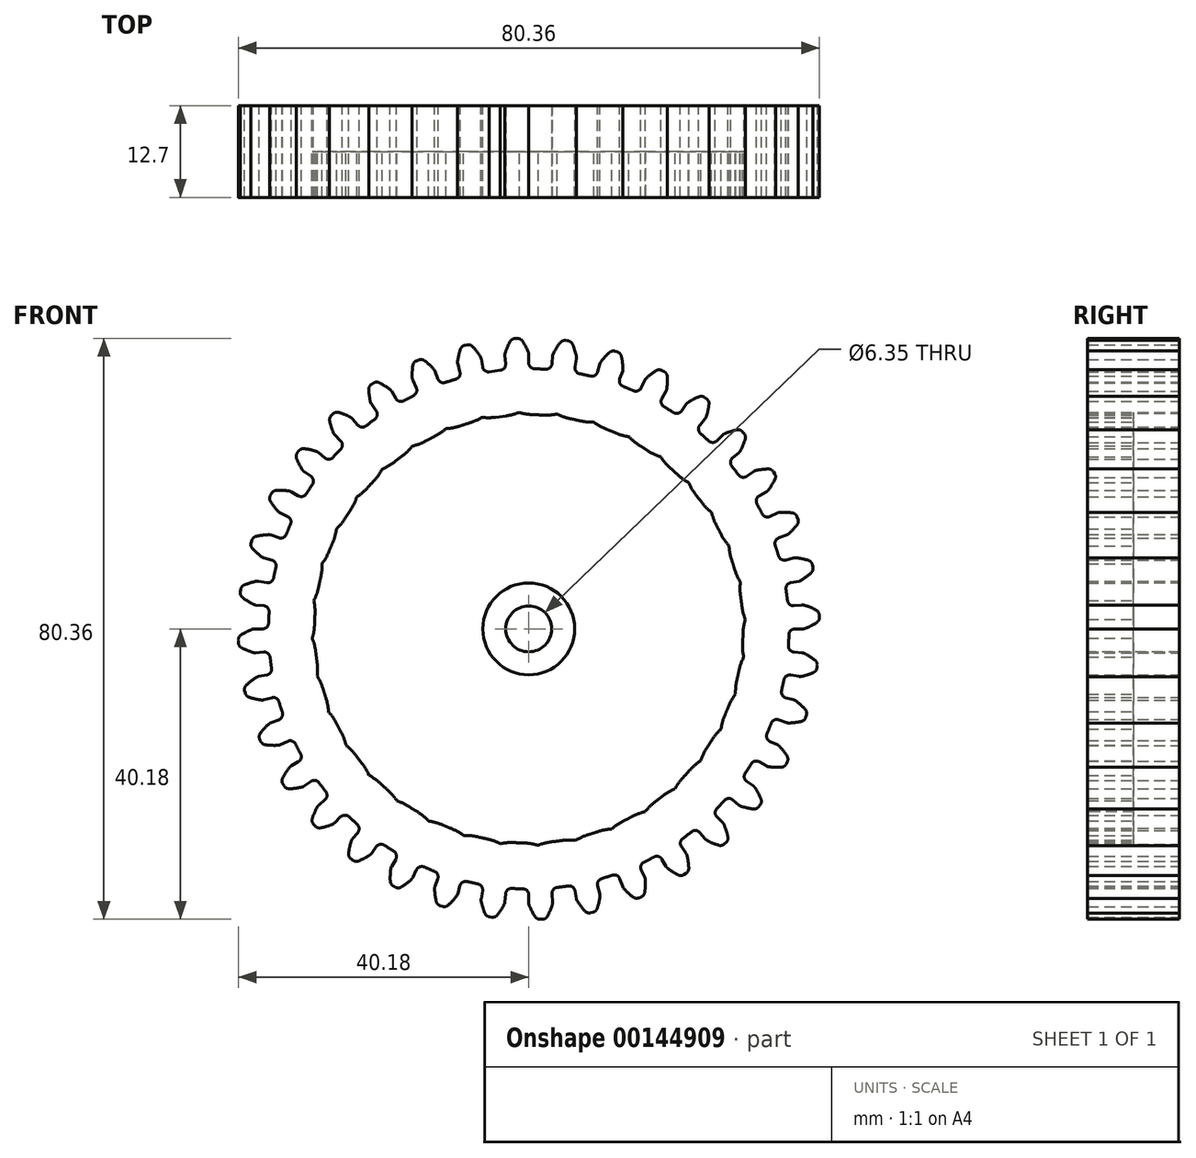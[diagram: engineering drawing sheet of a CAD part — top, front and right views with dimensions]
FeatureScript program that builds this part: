
annotation { "Feature Type Name" : "Feature", "Feature Type Description" : "" }
export const myFeature = defineFeature(function(context is Context, id is Id, definition is map)
    precondition{}
    {
        {
            var Q0;
            Q0=qCreatedBy(makeId("Front.planeOp"),FACE);
            var sketch = newSketch(context, id + "F0", { "sketchPlane" : qUnion([Q0])});
            skPoint(sketch, "E0.endSnap0", {"position": v(-3.06, 34.96) * mm});
            skArc(sketch, "E1.trimOffspring", {"start": v(-0.06, 38.25) * mm, "mid": v(-0.43, 39.05) * mm, "end": v(-0.86, 39.8) * mm});
            skLineSegment(sketch, "E2", {"start": v(0, 37.94) * mm, "end": v(0, 36.8) * mm});
            skLineSegment(sketch, "E3", {"start": v(-1.6, 40.18) * mm, "end": v(-1.75, 40.17) * mm});
            skArc(sketch, "E4.MirrorCS", {"start": v(-3.27, 38.11) * mm, "mid": v(-2.98, 38.93) * mm, "end": v(-2.61, 39.72) * mm});
            skLineSegment(sketch, "E5.MirrorCS", {"start": v(-1.91, 40.17) * mm, "end": v(-1.75, 40.17) * mm});
            skLineSegment(sketch, "E6.MirrorCS", {"start": v(-3.3, 37.8) * mm, "end": v(-3.2, 36.66) * mm});
            skPoint(sketch, "E7.visualSharp", {"position": v(0, 35.98) * mm});
            skArc(sketch, "E7.filletArc", {"start": v(0, 36.8) * mm, "mid": v(0.24, 36.22) * mm, "end": v(0.8, 35.97) * mm});
            skArc(sketch, "E8.filletArc", {"start": v(-0.86, 39.8) * mm, "mid": v(-1.18, 40.09) * mm, "end": v(-1.6, 40.18) * mm});
            skArc(sketch, "E9.filletArc", {"start": v(-1.91, 40.17) * mm, "mid": v(-2.32, 40.04) * mm, "end": v(-2.61, 39.72) * mm});
            skPoint(sketch, "E10.visualSharp", {"position": v(-3.32, 37.96) * mm});
            skArc(sketch, "E10.filletArc", {"start": v(-3.27, 38.11) * mm, "mid": v(-3.3, 37.96) * mm, "end": v(-3.3, 37.8) * mm});
            skPoint(sketch, "E11.visualSharp", {"position": v(-3.14, 35.85) * mm});
            skArc(sketch, "E11.filletArc", {"start": v(-3.94, 35.77) * mm, "mid": v(-3.4, 36.06) * mm, "end": v(-3.2, 36.66) * mm});
            skPoint(sketch, "E12.visualSharp", {"position": v(0, 38.1) * mm});
            skArc(sketch, "E12.filletArc", {"start": v(0, 37.94) * mm, "mid": v(-0.02, 38.1) * mm, "end": v(-0.06, 38.25) * mm});
            skArc(sketch, "E13.1.0", {"start": v(-10.1, 34.54) * mm, "mid": v(-9.6, 34.93) * mm, "end": v(-9.52, 35.55) * mm});
            skLineSegment(sketch, "E13.1.1", {"start": v(-9.82, 36.65) * mm, "end": v(-9.52, 35.55) * mm});
            skArc(sketch, "E13.1.2", {"start": v(-9.84, 36.97) * mm, "mid": v(-9.85, 36.8) * mm, "end": v(-9.82, 36.65) * mm});
            skArc(sketch, "E13.1.3", {"start": v(-9.84, 36.97) * mm, "mid": v(-9.7, 37.83) * mm, "end": v(-9.47, 38.67) * mm});
            skArc(sketch, "E13.1.4", {"start": v(-6.4, 36.24) * mm, "mid": v(-6.06, 35.71) * mm, "end": v(-5.45, 35.57) * mm});
            skLineSegment(sketch, "E13.1.5", {"start": v(-6.59, 37.37) * mm, "end": v(-6.4, 36.24) * mm});
            skArc(sketch, "E13.1.6", {"start": v(-6.59, 37.37) * mm, "mid": v(-6.63, 37.52) * mm, "end": v(-6.7, 37.66) * mm});
            skArc(sketch, "E13.1.7", {"start": v(-8.86, 39.22) * mm, "mid": v(-9.24, 39.03) * mm, "end": v(-9.47, 38.67) * mm});
            skArc(sketch, "E13.1.8", {"start": v(-7.76, 39.05) * mm, "mid": v(-8.12, 39.27) * mm, "end": v(-8.55, 39.3) * mm});
            skArc(sketch, "E13.1.9", {"start": v(-6.7, 37.66) * mm, "mid": v(-7.2, 38.38) * mm, "end": v(-7.76, 39.05) * mm});
            skLineSegment(sketch, "E13.1.10", {"start": v(-8.55, 39.3) * mm, "end": v(-8.7, 39.26) * mm});
            skLineSegment(sketch, "E13.1.11", {"start": v(-8.86, 39.22) * mm, "end": v(-8.7, 39.26) * mm});
            skArc(sketch, "E13.2.0", {"start": v(-15.93, 32.26) * mm, "mid": v(-15.52, 32.73) * mm, "end": v(-15.55, 33.35) * mm});
            skLineSegment(sketch, "E13.2.1", {"start": v(-16.04, 34.39) * mm, "end": v(-15.55, 33.35) * mm});
            skArc(sketch, "E13.2.2", {"start": v(-16.11, 34.7) * mm, "mid": v(-16.09, 34.54) * mm, "end": v(-16.04, 34.39) * mm});
            skArc(sketch, "E13.2.3", {"start": v(-16.11, 34.7) * mm, "mid": v(-16.12, 35.57) * mm, "end": v(-16.04, 36.44) * mm});
            skArc(sketch, "E13.2.4", {"start": v(-12.59, 34.58) * mm, "mid": v(-12.17, 34.12) * mm, "end": v(-11.55, 34.08) * mm});
            skLineSegment(sketch, "E13.2.5", {"start": v(-12.98, 35.65) * mm, "end": v(-12.59, 34.58) * mm});
            skArc(sketch, "E13.2.6", {"start": v(-12.98, 35.65) * mm, "mid": v(-13.05, 35.8) * mm, "end": v(-13.14, 35.93) * mm});
            skArc(sketch, "E13.2.7", {"start": v(-15.54, 37.09) * mm, "mid": v(-15.88, 36.83) * mm, "end": v(-16.04, 36.44) * mm});
            skArc(sketch, "E13.2.8", {"start": v(-14.42, 37.1) * mm, "mid": v(-14.82, 37.27) * mm, "end": v(-15.24, 37.21) * mm});
            skArc(sketch, "E13.2.9", {"start": v(-13.14, 35.93) * mm, "mid": v(-13.75, 36.54) * mm, "end": v(-14.42, 37.1) * mm});
            skLineSegment(sketch, "E13.2.10", {"start": v(-15.24, 37.21) * mm, "end": v(-15.39, 37.15) * mm});
            skLineSegment(sketch, "E13.2.11", {"start": v(-15.54, 37.09) * mm, "end": v(-15.39, 37.15) * mm});
            skArc(sketch, "E13.3.0", {"start": v(-21.3, 29) * mm, "mid": v(-20.97, 29.54) * mm, "end": v(-21.1, 30.14) * mm});
            skLineSegment(sketch, "E13.3.1", {"start": v(-21.76, 31.08) * mm, "end": v(-21.1, 30.14) * mm});
            skArc(sketch, "E13.3.2", {"start": v(-21.9, 31.37) * mm, "mid": v(-21.84, 31.22) * mm, "end": v(-21.76, 31.08) * mm});
            skArc(sketch, "E13.3.3", {"start": v(-21.9, 31.37) * mm, "mid": v(-22.05, 32.23) * mm, "end": v(-22.12, 33.1) * mm});
            skArc(sketch, "E13.3.4", {"start": v(-18.4, 31.87) * mm, "mid": v(-17.9, 31.49) * mm, "end": v(-17.29, 31.56) * mm});
            skLineSegment(sketch, "E13.3.5", {"start": v(-18.97, 32.86) * mm, "end": v(-18.4, 31.87) * mm});
            skArc(sketch, "E13.3.6", {"start": v(-18.97, 32.86) * mm, "mid": v(-19.06, 32.99) * mm, "end": v(-19.18, 33.1) * mm});
            skArc(sketch, "E13.3.7", {"start": v(-21.74, 33.83) * mm, "mid": v(-22.03, 33.51) * mm, "end": v(-22.12, 33.1) * mm});
            skArc(sketch, "E13.3.8", {"start": v(-20.65, 34.04) * mm, "mid": v(-21.06, 34.13) * mm, "end": v(-21.47, 34) * mm});
            skArc(sketch, "E13.3.9", {"start": v(-19.18, 33.1) * mm, "mid": v(-19.9, 33.6) * mm, "end": v(-20.65, 34.04) * mm});
            skLineSegment(sketch, "E13.3.10", {"start": v(-21.47, 34) * mm, "end": v(-21.6, 33.91) * mm});
            skLineSegment(sketch, "E13.3.11", {"start": v(-21.74, 33.83) * mm, "end": v(-21.6, 33.91) * mm});
            skArc(sketch, "E13.4.0", {"start": v(-26, 24.87) * mm, "mid": v(-25.78, 25.45) * mm, "end": v(-26.02, 26.02) * mm});
            skLineSegment(sketch, "E13.4.1", {"start": v(-26.83, 26.83) * mm, "end": v(-26.02, 26.02) * mm});
            skArc(sketch, "E13.4.2", {"start": v(-27, 27.1) * mm, "mid": v(-26.93, 26.95) * mm, "end": v(-26.83, 26.83) * mm});
            skArc(sketch, "E13.4.3", {"start": v(-27, 27.1) * mm, "mid": v(-27.3, 27.91) * mm, "end": v(-27.53, 28.75) * mm});
            skArc(sketch, "E13.4.4", {"start": v(-23.65, 28.2) * mm, "mid": v(-23.1, 27.9) * mm, "end": v(-22.5, 28.08) * mm});
            skLineSegment(sketch, "E13.4.5", {"start": v(-24.39, 29.07) * mm, "end": v(-23.65, 28.2) * mm});
            skArc(sketch, "E13.4.6", {"start": v(-24.39, 29.07) * mm, "mid": v(-24.5, 29.18) * mm, "end": v(-24.64, 29.26) * mm});
            skArc(sketch, "E13.4.7", {"start": v(-27.29, 29.54) * mm, "mid": v(-27.51, 29.18) * mm, "end": v(-27.53, 28.75) * mm});
            skArc(sketch, "E13.4.8", {"start": v(-26.24, 29.94) * mm, "mid": v(-26.67, 29.95) * mm, "end": v(-27.05, 29.76) * mm});
            skArc(sketch, "E13.4.9", {"start": v(-24.64, 29.26) * mm, "mid": v(-25.42, 29.64) * mm, "end": v(-26.24, 29.94) * mm});
            skLineSegment(sketch, "E13.4.10", {"start": v(-27.05, 29.76) * mm, "end": v(-27.17, 29.65) * mm});
            skLineSegment(sketch, "E13.4.11", {"start": v(-27.29, 29.54) * mm, "end": v(-27.17, 29.65) * mm});
            skArc(sketch, "E13.5.0", {"start": v(-29.93, 19.97) * mm, "mid": v(-29.8, 20.58) * mm, "end": v(-30.14, 21.1) * mm});
            skLineSegment(sketch, "E13.5.1", {"start": v(-31.08, 21.76) * mm, "end": v(-30.14, 21.1) * mm});
            skArc(sketch, "E13.5.2", {"start": v(-31.3, 22) * mm, "mid": v(-31.2, 21.87) * mm, "end": v(-31.08, 21.76) * mm});
            skArc(sketch, "E13.5.3", {"start": v(-31.3, 22) * mm, "mid": v(-31.74, 22.74) * mm, "end": v(-32.1, 23.53) * mm});
            skArc(sketch, "E13.5.4", {"start": v(-28.2, 23.65) * mm, "mid": v(-27.6, 23.46) * mm, "end": v(-27.04, 23.74) * mm});
            skLineSegment(sketch, "E13.5.5", {"start": v(-29.07, 24.39) * mm, "end": v(-28.2, 23.65) * mm});
            skArc(sketch, "E13.5.6", {"start": v(-29.07, 24.39) * mm, "mid": v(-29.2, 24.48) * mm, "end": v(-29.34, 24.54) * mm});
            skArc(sketch, "E13.5.7", {"start": v(-32, 24.35) * mm, "mid": v(-32.16, 23.96) * mm, "end": v(-32.1, 23.53) * mm});
            skArc(sketch, "E13.5.8", {"start": v(-31.04, 24.92) * mm, "mid": v(-31.47, 24.87) * mm, "end": v(-31.8, 24.6) * mm});
            skArc(sketch, "E13.5.9", {"start": v(-29.34, 24.54) * mm, "mid": v(-30.18, 24.77) * mm, "end": v(-31.04, 24.92) * mm});
            skLineSegment(sketch, "E13.5.10", {"start": v(-31.8, 24.6) * mm, "end": v(-31.9, 24.48) * mm});
            skLineSegment(sketch, "E13.5.11", {"start": v(-32, 24.35) * mm, "end": v(-31.9, 24.48) * mm});
            skArc(sketch, "E13.6.0", {"start": v(-32.94, 14.47) * mm, "mid": v(-32.93, 15.1) * mm, "end": v(-33.35, 15.55) * mm});
            skLineSegment(sketch, "E13.6.1", {"start": v(-34.39, 16.04) * mm, "end": v(-33.35, 15.55) * mm});
            skArc(sketch, "E13.6.2", {"start": v(-34.64, 16.22) * mm, "mid": v(-34.52, 16.12) * mm, "end": v(-34.39, 16.04) * mm});
            skArc(sketch, "E13.6.3", {"start": v(-34.64, 16.22) * mm, "mid": v(-35.2, 16.89) * mm, "end": v(-35.7, 17.6) * mm});
            skArc(sketch, "E13.6.4", {"start": v(-31.87, 18.4) * mm, "mid": v(-31.25, 18.31) * mm, "end": v(-30.75, 18.69) * mm});
            skLineSegment(sketch, "E13.6.5", {"start": v(-32.86, 18.97) * mm, "end": v(-31.87, 18.4) * mm});
            skArc(sketch, "E13.6.6", {"start": v(-32.86, 18.97) * mm, "mid": v(-33, 19.04) * mm, "end": v(-33.16, 19.07) * mm});
            skArc(sketch, "E13.6.7", {"start": v(-35.74, 18.42) * mm, "mid": v(-35.83, 18) * mm, "end": v(-35.7, 17.6) * mm});
            skArc(sketch, "E13.6.8", {"start": v(-34.9, 19.15) * mm, "mid": v(-35.3, 19.03) * mm, "end": v(-35.6, 18.71) * mm});
            skArc(sketch, "E13.6.9", {"start": v(-33.16, 19.07) * mm, "mid": v(-34.03, 19.15) * mm, "end": v(-34.9, 19.15) * mm});
            skLineSegment(sketch, "E13.6.10", {"start": v(-35.6, 18.71) * mm, "end": v(-35.67, 18.57) * mm});
            skLineSegment(sketch, "E13.6.11", {"start": v(-35.74, 18.42) * mm, "end": v(-35.67, 18.57) * mm});
            skArc(sketch, "E13.7.0", {"start": v(-34.96, 8.53) * mm, "mid": v(-35.05, 9.15) * mm, "end": v(-35.55, 9.52) * mm});
            skLineSegment(sketch, "E13.7.1", {"start": v(-36.65, 9.82) * mm, "end": v(-35.55, 9.52) * mm});
            skArc(sketch, "E13.7.2", {"start": v(-36.93, 9.96) * mm, "mid": v(-36.8, 9.88) * mm, "end": v(-36.65, 9.82) * mm});
            skArc(sketch, "E13.7.3", {"start": v(-36.93, 9.96) * mm, "mid": v(-37.6, 10.52) * mm, "end": v(-38.22, 11.13) * mm});
            skArc(sketch, "E13.7.4", {"start": v(-34.58, 12.59) * mm, "mid": v(-33.96, 12.6) * mm, "end": v(-33.53, 13.06) * mm});
            skLineSegment(sketch, "E13.7.5", {"start": v(-35.65, 12.98) * mm, "end": v(-34.58, 12.59) * mm});
            skArc(sketch, "E13.7.6", {"start": v(-35.65, 12.98) * mm, "mid": v(-35.8, 13.02) * mm, "end": v(-35.97, 13.03) * mm});
            skArc(sketch, "E13.7.7", {"start": v(-38.4, 11.94) * mm, "mid": v(-38.42, 11.51) * mm, "end": v(-38.22, 11.13) * mm});
            skArc(sketch, "E13.7.8", {"start": v(-37.7, 12.8) * mm, "mid": v(-38.07, 12.6) * mm, "end": v(-38.3, 12.25) * mm});
            skArc(sketch, "E13.7.9", {"start": v(-35.97, 13.03) * mm, "mid": v(-36.84, 12.95) * mm, "end": v(-37.7, 12.8) * mm});
            skLineSegment(sketch, "E13.7.10", {"start": v(-38.3, 12.25) * mm, "end": v(-38.35, 12.1) * mm});
            skLineSegment(sketch, "E13.7.11", {"start": v(-38.4, 11.94) * mm, "end": v(-38.35, 12.1) * mm});
            skArc(sketch, "E13.8.0", {"start": v(-35.9, 2.33) * mm, "mid": v(-36.1, 2.92) * mm, "end": v(-36.66, 3.2) * mm});
            skLineSegment(sketch, "E13.8.1", {"start": v(-37.8, 3.3) * mm, "end": v(-36.66, 3.2) * mm});
            skArc(sketch, "E13.8.2", {"start": v(-38.1, 3.4) * mm, "mid": v(-37.95, 3.34) * mm, "end": v(-37.8, 3.3) * mm});
            skArc(sketch, "E13.8.3", {"start": v(-38.1, 3.4) * mm, "mid": v(-38.86, 3.83) * mm, "end": v(-39.57, 4.33) * mm});
            skArc(sketch, "E13.8.4", {"start": v(-36.24, 6.4) * mm, "mid": v(-35.63, 6.52) * mm, "end": v(-35.29, 7.04) * mm});
            skLineSegment(sketch, "E13.8.5", {"start": v(-37.37, 6.59) * mm, "end": v(-36.24, 6.4) * mm});
            skArc(sketch, "E13.8.6", {"start": v(-37.37, 6.59) * mm, "mid": v(-37.52, 6.6) * mm, "end": v(-37.68, 6.58) * mm});
            skArc(sketch, "E13.8.7", {"start": v(-39.89, 5.09) * mm, "mid": v(-39.83, 4.67) * mm, "end": v(-39.57, 4.33) * mm});
            skArc(sketch, "E13.8.8", {"start": v(-39.35, 6.06) * mm, "mid": v(-39.68, 5.8) * mm, "end": v(-39.85, 5.4) * mm});
            skArc(sketch, "E13.8.9", {"start": v(-37.68, 6.58) * mm, "mid": v(-38.53, 6.36) * mm, "end": v(-39.35, 6.06) * mm});
            skLineSegment(sketch, "E13.8.10", {"start": v(-39.85, 5.4) * mm, "end": v(-39.87, 5.25) * mm});
            skLineSegment(sketch, "E13.8.11", {"start": v(-39.89, 5.09) * mm, "end": v(-39.87, 5.25) * mm});
            skArc(sketch, "E13.9.0", {"start": v(-35.77, -3.94) * mm, "mid": v(-36.06, -3.4) * mm, "end": v(-36.66, -3.2) * mm});
            skLineSegment(sketch, "E13.9.1", {"start": v(-37.8, -3.3) * mm, "end": v(-36.66, -3.2) * mm});
            skArc(sketch, "E13.9.2", {"start": v(-38.11, -3.27) * mm, "mid": v(-37.96, -3.3) * mm, "end": v(-37.8, -3.3) * mm});
            skArc(sketch, "E13.9.3", {"start": v(-38.11, -3.27) * mm, "mid": v(-38.93, -2.98) * mm, "end": v(-39.72, -2.61) * mm});
            skArc(sketch, "E13.9.4", {"start": v(-36.8, 0) * mm, "mid": v(-36.22, 0.24) * mm, "end": v(-35.97, 0.8) * mm});
            skLineSegment(sketch, "E13.9.5", {"start": v(-37.94, 0) * mm, "end": v(-36.8, 0) * mm});
            skArc(sketch, "E13.9.6", {"start": v(-37.94, 0) * mm, "mid": v(-38.1, -0.02) * mm, "end": v(-38.25, -0.06) * mm});
            skArc(sketch, "E13.9.7", {"start": v(-40.17, -1.91) * mm, "mid": v(-40.04, -2.32) * mm, "end": v(-39.72, -2.61) * mm});
            skArc(sketch, "E13.9.8", {"start": v(-39.8, -0.86) * mm, "mid": v(-40.09, -1.18) * mm, "end": v(-40.18, -1.6) * mm});
            skArc(sketch, "E13.9.9", {"start": v(-38.25, -0.06) * mm, "mid": v(-39.05, -0.43) * mm, "end": v(-39.8, -0.86) * mm});
            skLineSegment(sketch, "E13.9.10", {"start": v(-40.18, -1.6) * mm, "end": v(-40.17, -1.75) * mm});
            skLineSegment(sketch, "E13.9.11", {"start": v(-40.17, -1.91) * mm, "end": v(-40.17, -1.75) * mm});
            skArc(sketch, "E13.10.0", {"start": v(-34.54, -10.1) * mm, "mid": v(-34.93, -9.6) * mm, "end": v(-35.55, -9.52) * mm});
            skLineSegment(sketch, "E13.10.1", {"start": v(-36.65, -9.82) * mm, "end": v(-35.55, -9.52) * mm});
            skArc(sketch, "E13.10.2", {"start": v(-36.97, -9.84) * mm, "mid": v(-36.8, -9.85) * mm, "end": v(-36.65, -9.82) * mm});
            skArc(sketch, "E13.10.3", {"start": v(-36.97, -9.84) * mm, "mid": v(-37.83, -9.7) * mm, "end": v(-38.67, -9.47) * mm});
            skArc(sketch, "E13.10.4", {"start": v(-36.24, -6.4) * mm, "mid": v(-35.71, -6.06) * mm, "end": v(-35.57, -5.45) * mm});
            skLineSegment(sketch, "E13.10.5", {"start": v(-37.37, -6.59) * mm, "end": v(-36.24, -6.4) * mm});
            skArc(sketch, "E13.10.6", {"start": v(-37.37, -6.59) * mm, "mid": v(-37.52, -6.63) * mm, "end": v(-37.66, -6.7) * mm});
            skArc(sketch, "E13.10.7", {"start": v(-39.22, -8.86) * mm, "mid": v(-39.03, -9.24) * mm, "end": v(-38.67, -9.47) * mm});
            skArc(sketch, "E13.10.8", {"start": v(-39.05, -7.76) * mm, "mid": v(-39.27, -8.12) * mm, "end": v(-39.3, -8.55) * mm});
            skArc(sketch, "E13.10.9", {"start": v(-37.66, -6.7) * mm, "mid": v(-38.38, -7.2) * mm, "end": v(-39.05, -7.76) * mm});
            skLineSegment(sketch, "E13.10.10", {"start": v(-39.3, -8.55) * mm, "end": v(-39.26, -8.7) * mm});
            skLineSegment(sketch, "E13.10.11", {"start": v(-39.22, -8.86) * mm, "end": v(-39.26, -8.7) * mm});
            skArc(sketch, "E13.11.0", {"start": v(-32.26, -15.93) * mm, "mid": v(-32.73, -15.52) * mm, "end": v(-33.35, -15.55) * mm});
            skLineSegment(sketch, "E13.11.1", {"start": v(-34.39, -16.04) * mm, "end": v(-33.35, -15.55) * mm});
            skArc(sketch, "E13.11.2", {"start": v(-34.7, -16.11) * mm, "mid": v(-34.54, -16.09) * mm, "end": v(-34.39, -16.04) * mm});
            skArc(sketch, "E13.11.3", {"start": v(-34.7, -16.11) * mm, "mid": v(-35.57, -16.12) * mm, "end": v(-36.44, -16.04) * mm});
            skArc(sketch, "E13.11.4", {"start": v(-34.58, -12.59) * mm, "mid": v(-34.12, -12.17) * mm, "end": v(-34.08, -11.55) * mm});
            skLineSegment(sketch, "E13.11.5", {"start": v(-35.65, -12.98) * mm, "end": v(-34.58, -12.59) * mm});
            skArc(sketch, "E13.11.6", {"start": v(-35.65, -12.98) * mm, "mid": v(-35.8, -13.05) * mm, "end": v(-35.93, -13.14) * mm});
            skArc(sketch, "E13.11.7", {"start": v(-37.09, -15.54) * mm, "mid": v(-36.83, -15.88) * mm, "end": v(-36.44, -16.04) * mm});
            skArc(sketch, "E13.11.8", {"start": v(-37.1, -14.42) * mm, "mid": v(-37.27, -14.82) * mm, "end": v(-37.21, -15.24) * mm});
            skArc(sketch, "E13.11.9", {"start": v(-35.93, -13.14) * mm, "mid": v(-36.54, -13.75) * mm, "end": v(-37.1, -14.42) * mm});
            skLineSegment(sketch, "E13.11.10", {"start": v(-37.21, -15.24) * mm, "end": v(-37.15, -15.39) * mm});
            skLineSegment(sketch, "E13.11.11", {"start": v(-37.09, -15.54) * mm, "end": v(-37.15, -15.39) * mm});
            skArc(sketch, "E13.12.0", {"start": v(-29, -21.3) * mm, "mid": v(-29.54, -20.97) * mm, "end": v(-30.14, -21.1) * mm});
            skLineSegment(sketch, "E13.12.1", {"start": v(-31.08, -21.76) * mm, "end": v(-30.14, -21.1) * mm});
            skArc(sketch, "E13.12.2", {"start": v(-31.37, -21.9) * mm, "mid": v(-31.22, -21.84) * mm, "end": v(-31.08, -21.76) * mm});
            skArc(sketch, "E13.12.3", {"start": v(-31.37, -21.9) * mm, "mid": v(-32.23, -22.05) * mm, "end": v(-33.1, -22.12) * mm});
            skArc(sketch, "E13.12.4", {"start": v(-31.87, -18.4) * mm, "mid": v(-31.49, -17.9) * mm, "end": v(-31.56, -17.29) * mm});
            skLineSegment(sketch, "E13.12.5", {"start": v(-32.86, -18.97) * mm, "end": v(-31.87, -18.4) * mm});
            skArc(sketch, "E13.12.6", {"start": v(-32.86, -18.97) * mm, "mid": v(-32.99, -19.06) * mm, "end": v(-33.1, -19.18) * mm});
            skArc(sketch, "E13.12.7", {"start": v(-33.83, -21.74) * mm, "mid": v(-33.51, -22.03) * mm, "end": v(-33.1, -22.12) * mm});
            skArc(sketch, "E13.12.8", {"start": v(-34.04, -20.65) * mm, "mid": v(-34.13, -21.06) * mm, "end": v(-34, -21.47) * mm});
            skArc(sketch, "E13.12.9", {"start": v(-33.1, -19.18) * mm, "mid": v(-33.6, -19.9) * mm, "end": v(-34.04, -20.65) * mm});
            skLineSegment(sketch, "E13.12.10", {"start": v(-34, -21.47) * mm, "end": v(-33.91, -21.6) * mm});
            skLineSegment(sketch, "E13.12.11", {"start": v(-33.83, -21.74) * mm, "end": v(-33.91, -21.6) * mm});
            skArc(sketch, "E13.13.0", {"start": v(-24.87, -26) * mm, "mid": v(-25.45, -25.78) * mm, "end": v(-26.02, -26.02) * mm});
            skLineSegment(sketch, "E13.13.1", {"start": v(-26.83, -26.83) * mm, "end": v(-26.02, -26.02) * mm});
            skArc(sketch, "E13.13.2", {"start": v(-27.1, -27) * mm, "mid": v(-26.95, -26.93) * mm, "end": v(-26.83, -26.83) * mm});
            skArc(sketch, "E13.13.3", {"start": v(-27.1, -27) * mm, "mid": v(-27.91, -27.3) * mm, "end": v(-28.75, -27.53) * mm});
            skArc(sketch, "E13.13.4", {"start": v(-28.2, -23.65) * mm, "mid": v(-27.9, -23.1) * mm, "end": v(-28.08, -22.5) * mm});
            skLineSegment(sketch, "E13.13.5", {"start": v(-29.07, -24.39) * mm, "end": v(-28.2, -23.65) * mm});
            skArc(sketch, "E13.13.6", {"start": v(-29.07, -24.39) * mm, "mid": v(-29.18, -24.5) * mm, "end": v(-29.26, -24.64) * mm});
            skArc(sketch, "E13.13.7", {"start": v(-29.54, -27.29) * mm, "mid": v(-29.18, -27.51) * mm, "end": v(-28.75, -27.53) * mm});
            skArc(sketch, "E13.13.8", {"start": v(-29.94, -26.24) * mm, "mid": v(-29.95, -26.67) * mm, "end": v(-29.76, -27.05) * mm});
            skArc(sketch, "E13.13.9", {"start": v(-29.26, -24.64) * mm, "mid": v(-29.64, -25.42) * mm, "end": v(-29.94, -26.24) * mm});
            skLineSegment(sketch, "E13.13.10", {"start": v(-29.76, -27.05) * mm, "end": v(-29.65, -27.17) * mm});
            skLineSegment(sketch, "E13.13.11", {"start": v(-29.54, -27.29) * mm, "end": v(-29.65, -27.17) * mm});
            skArc(sketch, "E13.14.0", {"start": v(-19.97, -29.93) * mm, "mid": v(-20.58, -29.8) * mm, "end": v(-21.1, -30.14) * mm});
            skLineSegment(sketch, "E13.14.1", {"start": v(-21.76, -31.08) * mm, "end": v(-21.1, -30.14) * mm});
            skArc(sketch, "E13.14.2", {"start": v(-22, -31.3) * mm, "mid": v(-21.87, -31.2) * mm, "end": v(-21.76, -31.08) * mm});
            skArc(sketch, "E13.14.3", {"start": v(-22, -31.3) * mm, "mid": v(-22.74, -31.74) * mm, "end": v(-23.53, -32.1) * mm});
            skArc(sketch, "E13.14.4", {"start": v(-23.65, -28.2) * mm, "mid": v(-23.46, -27.6) * mm, "end": v(-23.74, -27.04) * mm});
            skLineSegment(sketch, "E13.14.5", {"start": v(-24.39, -29.07) * mm, "end": v(-23.65, -28.2) * mm});
            skArc(sketch, "E13.14.6", {"start": v(-24.39, -29.07) * mm, "mid": v(-24.48, -29.2) * mm, "end": v(-24.54, -29.34) * mm});
            skArc(sketch, "E13.14.7", {"start": v(-24.35, -32) * mm, "mid": v(-23.96, -32.16) * mm, "end": v(-23.53, -32.1) * mm});
            skArc(sketch, "E13.14.8", {"start": v(-24.92, -31.04) * mm, "mid": v(-24.87, -31.47) * mm, "end": v(-24.6, -31.8) * mm});
            skArc(sketch, "E13.14.9", {"start": v(-24.54, -29.34) * mm, "mid": v(-24.77, -30.18) * mm, "end": v(-24.92, -31.04) * mm});
            skLineSegment(sketch, "E13.14.10", {"start": v(-24.6, -31.8) * mm, "end": v(-24.48, -31.9) * mm});
            skLineSegment(sketch, "E13.14.11", {"start": v(-24.35, -32) * mm, "end": v(-24.48, -31.9) * mm});
            skArc(sketch, "E13.15.0", {"start": v(-14.47, -32.94) * mm, "mid": v(-15.1, -32.93) * mm, "end": v(-15.55, -33.35) * mm});
            skLineSegment(sketch, "E13.15.1", {"start": v(-16.04, -34.39) * mm, "end": v(-15.55, -33.35) * mm});
            skArc(sketch, "E13.15.2", {"start": v(-16.22, -34.64) * mm, "mid": v(-16.12, -34.52) * mm, "end": v(-16.04, -34.39) * mm});
            skArc(sketch, "E13.15.3", {"start": v(-16.22, -34.64) * mm, "mid": v(-16.89, -35.2) * mm, "end": v(-17.6, -35.7) * mm});
            skArc(sketch, "E13.15.4", {"start": v(-18.4, -31.87) * mm, "mid": v(-18.31, -31.25) * mm, "end": v(-18.69, -30.75) * mm});
            skLineSegment(sketch, "E13.15.5", {"start": v(-18.97, -32.86) * mm, "end": v(-18.4, -31.87) * mm});
            skArc(sketch, "E13.15.6", {"start": v(-18.97, -32.86) * mm, "mid": v(-19.04, -33) * mm, "end": v(-19.07, -33.16) * mm});
            skArc(sketch, "E13.15.7", {"start": v(-18.42, -35.74) * mm, "mid": v(-18, -35.83) * mm, "end": v(-17.6, -35.7) * mm});
            skArc(sketch, "E13.15.8", {"start": v(-19.15, -34.9) * mm, "mid": v(-19.03, -35.3) * mm, "end": v(-18.71, -35.6) * mm});
            skArc(sketch, "E13.15.9", {"start": v(-19.07, -33.16) * mm, "mid": v(-19.15, -34.03) * mm, "end": v(-19.15, -34.9) * mm});
            skLineSegment(sketch, "E13.15.10", {"start": v(-18.71, -35.6) * mm, "end": v(-18.57, -35.67) * mm});
            skLineSegment(sketch, "E13.15.11", {"start": v(-18.42, -35.74) * mm, "end": v(-18.57, -35.67) * mm});
            skArc(sketch, "E13.16.0", {"start": v(-8.53, -34.96) * mm, "mid": v(-9.15, -35.05) * mm, "end": v(-9.52, -35.55) * mm});
            skLineSegment(sketch, "E13.16.1", {"start": v(-9.82, -36.65) * mm, "end": v(-9.52, -35.55) * mm});
            skArc(sketch, "E13.16.2", {"start": v(-9.96, -36.93) * mm, "mid": v(-9.88, -36.8) * mm, "end": v(-9.82, -36.65) * mm});
            skArc(sketch, "E13.16.3", {"start": v(-9.96, -36.93) * mm, "mid": v(-10.52, -37.6) * mm, "end": v(-11.13, -38.22) * mm});
            skArc(sketch, "E13.16.4", {"start": v(-12.59, -34.58) * mm, "mid": v(-12.6, -33.96) * mm, "end": v(-13.06, -33.53) * mm});
            skLineSegment(sketch, "E13.16.5", {"start": v(-12.98, -35.65) * mm, "end": v(-12.59, -34.58) * mm});
            skArc(sketch, "E13.16.6", {"start": v(-12.98, -35.65) * mm, "mid": v(-13.02, -35.8) * mm, "end": v(-13.03, -35.97) * mm});
            skArc(sketch, "E13.16.7", {"start": v(-11.94, -38.4) * mm, "mid": v(-11.51, -38.42) * mm, "end": v(-11.13, -38.22) * mm});
            skArc(sketch, "E13.16.8", {"start": v(-12.8, -37.7) * mm, "mid": v(-12.6, -38.07) * mm, "end": v(-12.25, -38.3) * mm});
            skArc(sketch, "E13.16.9", {"start": v(-13.03, -35.97) * mm, "mid": v(-12.95, -36.84) * mm, "end": v(-12.8, -37.7) * mm});
            skLineSegment(sketch, "E13.16.10", {"start": v(-12.25, -38.3) * mm, "end": v(-12.1, -38.35) * mm});
            skLineSegment(sketch, "E13.16.11", {"start": v(-11.94, -38.4) * mm, "end": v(-12.1, -38.35) * mm});
            skArc(sketch, "E13.17.0", {"start": v(-2.33, -35.9) * mm, "mid": v(-2.92, -36.1) * mm, "end": v(-3.2, -36.66) * mm});
            skLineSegment(sketch, "E13.17.1", {"start": v(-3.3, -37.8) * mm, "end": v(-3.2, -36.66) * mm});
            skArc(sketch, "E13.17.2", {"start": v(-3.4, -38.1) * mm, "mid": v(-3.34, -37.95) * mm, "end": v(-3.3, -37.8) * mm});
            skArc(sketch, "E13.17.3", {"start": v(-3.4, -38.1) * mm, "mid": v(-3.83, -38.86) * mm, "end": v(-4.33, -39.57) * mm});
            skArc(sketch, "E13.17.4", {"start": v(-6.4, -36.24) * mm, "mid": v(-6.52, -35.63) * mm, "end": v(-7.04, -35.29) * mm});
            skLineSegment(sketch, "E13.17.5", {"start": v(-6.59, -37.37) * mm, "end": v(-6.4, -36.24) * mm});
            skArc(sketch, "E13.17.6", {"start": v(-6.59, -37.37) * mm, "mid": v(-6.6, -37.52) * mm, "end": v(-6.58, -37.68) * mm});
            skArc(sketch, "E13.17.7", {"start": v(-5.09, -39.89) * mm, "mid": v(-4.67, -39.83) * mm, "end": v(-4.33, -39.57) * mm});
            skArc(sketch, "E13.17.8", {"start": v(-6.06, -39.35) * mm, "mid": v(-5.8, -39.68) * mm, "end": v(-5.4, -39.85) * mm});
            skArc(sketch, "E13.17.9", {"start": v(-6.58, -37.68) * mm, "mid": v(-6.36, -38.53) * mm, "end": v(-6.06, -39.35) * mm});
            skLineSegment(sketch, "E13.17.10", {"start": v(-5.4, -39.85) * mm, "end": v(-5.25, -39.87) * mm});
            skLineSegment(sketch, "E13.17.11", {"start": v(-5.09, -39.89) * mm, "end": v(-5.25, -39.87) * mm});
            skArc(sketch, "E13.18.0", {"start": v(3.94, -35.77) * mm, "mid": v(3.4, -36.06) * mm, "end": v(3.2, -36.66) * mm});
            skLineSegment(sketch, "E13.18.1", {"start": v(3.3, -37.8) * mm, "end": v(3.2, -36.66) * mm});
            skArc(sketch, "E13.18.2", {"start": v(3.27, -38.11) * mm, "mid": v(3.3, -37.96) * mm, "end": v(3.3, -37.8) * mm});
            skArc(sketch, "E13.18.3", {"start": v(3.27, -38.11) * mm, "mid": v(2.98, -38.93) * mm, "end": v(2.61, -39.72) * mm});
            skArc(sketch, "E13.18.4", {"start": v(0, -36.8) * mm, "mid": v(-0.24, -36.22) * mm, "end": v(-0.8, -35.97) * mm});
            skLineSegment(sketch, "E13.18.5", {"start": v(0, -37.94) * mm, "end": v(0, -36.8) * mm});
            skArc(sketch, "E13.18.6", {"start": v(0, -37.94) * mm, "mid": v(0.02, -38.1) * mm, "end": v(0.06, -38.25) * mm});
            skArc(sketch, "E13.18.7", {"start": v(1.91, -40.17) * mm, "mid": v(2.32, -40.04) * mm, "end": v(2.61, -39.72) * mm});
            skArc(sketch, "E13.18.8", {"start": v(0.86, -39.8) * mm, "mid": v(1.18, -40.09) * mm, "end": v(1.6, -40.18) * mm});
            skArc(sketch, "E13.18.9", {"start": v(0.06, -38.25) * mm, "mid": v(0.43, -39.05) * mm, "end": v(0.86, -39.8) * mm});
            skLineSegment(sketch, "E13.18.10", {"start": v(1.6, -40.18) * mm, "end": v(1.75, -40.17) * mm});
            skLineSegment(sketch, "E13.18.11", {"start": v(1.91, -40.17) * mm, "end": v(1.75, -40.17) * mm});
            skArc(sketch, "E13.19.0", {"start": v(10.1, -34.54) * mm, "mid": v(9.6, -34.93) * mm, "end": v(9.52, -35.55) * mm});
            skLineSegment(sketch, "E13.19.1", {"start": v(9.82, -36.65) * mm, "end": v(9.52, -35.55) * mm});
            skArc(sketch, "E13.19.2", {"start": v(9.84, -36.97) * mm, "mid": v(9.85, -36.8) * mm, "end": v(9.82, -36.65) * mm});
            skArc(sketch, "E13.19.3", {"start": v(9.84, -36.97) * mm, "mid": v(9.7, -37.83) * mm, "end": v(9.47, -38.67) * mm});
            skArc(sketch, "E13.19.4", {"start": v(6.4, -36.24) * mm, "mid": v(6.06, -35.71) * mm, "end": v(5.45, -35.57) * mm});
            skLineSegment(sketch, "E13.19.5", {"start": v(6.59, -37.37) * mm, "end": v(6.4, -36.24) * mm});
            skArc(sketch, "E13.19.6", {"start": v(6.59, -37.37) * mm, "mid": v(6.63, -37.52) * mm, "end": v(6.7, -37.66) * mm});
            skArc(sketch, "E13.19.7", {"start": v(8.86, -39.22) * mm, "mid": v(9.24, -39.03) * mm, "end": v(9.47, -38.67) * mm});
            skArc(sketch, "E13.19.8", {"start": v(7.76, -39.05) * mm, "mid": v(8.12, -39.27) * mm, "end": v(8.55, -39.3) * mm});
            skArc(sketch, "E13.19.9", {"start": v(6.7, -37.66) * mm, "mid": v(7.2, -38.38) * mm, "end": v(7.76, -39.05) * mm});
            skLineSegment(sketch, "E13.19.10", {"start": v(8.55, -39.3) * mm, "end": v(8.7, -39.26) * mm});
            skLineSegment(sketch, "E13.19.11", {"start": v(8.86, -39.22) * mm, "end": v(8.7, -39.26) * mm});
            skArc(sketch, "E13.20.0", {"start": v(15.93, -32.26) * mm, "mid": v(15.52, -32.73) * mm, "end": v(15.55, -33.35) * mm});
            skLineSegment(sketch, "E13.20.1", {"start": v(16.04, -34.39) * mm, "end": v(15.55, -33.35) * mm});
            skArc(sketch, "E13.20.2", {"start": v(16.11, -34.7) * mm, "mid": v(16.09, -34.54) * mm, "end": v(16.04, -34.39) * mm});
            skArc(sketch, "E13.20.3", {"start": v(16.11, -34.7) * mm, "mid": v(16.12, -35.57) * mm, "end": v(16.04, -36.44) * mm});
            skArc(sketch, "E13.20.4", {"start": v(12.59, -34.58) * mm, "mid": v(12.17, -34.12) * mm, "end": v(11.55, -34.08) * mm});
            skLineSegment(sketch, "E13.20.5", {"start": v(12.98, -35.65) * mm, "end": v(12.59, -34.58) * mm});
            skArc(sketch, "E13.20.6", {"start": v(12.98, -35.65) * mm, "mid": v(13.05, -35.8) * mm, "end": v(13.14, -35.93) * mm});
            skArc(sketch, "E13.20.7", {"start": v(15.54, -37.09) * mm, "mid": v(15.88, -36.83) * mm, "end": v(16.04, -36.44) * mm});
            skArc(sketch, "E13.20.8", {"start": v(14.42, -37.1) * mm, "mid": v(14.82, -37.27) * mm, "end": v(15.24, -37.21) * mm});
            skArc(sketch, "E13.20.9", {"start": v(13.14, -35.93) * mm, "mid": v(13.75, -36.54) * mm, "end": v(14.42, -37.1) * mm});
            skLineSegment(sketch, "E13.20.10", {"start": v(15.24, -37.21) * mm, "end": v(15.39, -37.15) * mm});
            skLineSegment(sketch, "E13.20.11", {"start": v(15.54, -37.09) * mm, "end": v(15.39, -37.15) * mm});
            skArc(sketch, "E13.21.0", {"start": v(21.3, -29) * mm, "mid": v(20.97, -29.54) * mm, "end": v(21.1, -30.14) * mm});
            skLineSegment(sketch, "E13.21.1", {"start": v(21.76, -31.08) * mm, "end": v(21.1, -30.14) * mm});
            skArc(sketch, "E13.21.2", {"start": v(21.9, -31.37) * mm, "mid": v(21.84, -31.22) * mm, "end": v(21.76, -31.08) * mm});
            skArc(sketch, "E13.21.3", {"start": v(21.9, -31.37) * mm, "mid": v(22.05, -32.23) * mm, "end": v(22.12, -33.1) * mm});
            skArc(sketch, "E13.21.4", {"start": v(18.4, -31.87) * mm, "mid": v(17.9, -31.49) * mm, "end": v(17.29, -31.56) * mm});
            skLineSegment(sketch, "E13.21.5", {"start": v(18.97, -32.86) * mm, "end": v(18.4, -31.87) * mm});
            skArc(sketch, "E13.21.6", {"start": v(18.97, -32.86) * mm, "mid": v(19.06, -32.99) * mm, "end": v(19.18, -33.1) * mm});
            skArc(sketch, "E13.21.7", {"start": v(21.74, -33.83) * mm, "mid": v(22.03, -33.51) * mm, "end": v(22.12, -33.1) * mm});
            skArc(sketch, "E13.21.8", {"start": v(20.65, -34.04) * mm, "mid": v(21.06, -34.13) * mm, "end": v(21.47, -34) * mm});
            skArc(sketch, "E13.21.9", {"start": v(19.18, -33.1) * mm, "mid": v(19.9, -33.6) * mm, "end": v(20.65, -34.04) * mm});
            skLineSegment(sketch, "E13.21.10", {"start": v(21.47, -34) * mm, "end": v(21.6, -33.91) * mm});
            skLineSegment(sketch, "E13.21.11", {"start": v(21.74, -33.83) * mm, "end": v(21.6, -33.91) * mm});
            skArc(sketch, "E13.22.0", {"start": v(26, -24.87) * mm, "mid": v(25.78, -25.45) * mm, "end": v(26.02, -26.02) * mm});
            skLineSegment(sketch, "E13.22.1", {"start": v(26.83, -26.83) * mm, "end": v(26.02, -26.02) * mm});
            skArc(sketch, "E13.22.2", {"start": v(27, -27.1) * mm, "mid": v(26.93, -26.95) * mm, "end": v(26.83, -26.83) * mm});
            skArc(sketch, "E13.22.3", {"start": v(27, -27.1) * mm, "mid": v(27.3, -27.91) * mm, "end": v(27.53, -28.75) * mm});
            skArc(sketch, "E13.22.4", {"start": v(23.65, -28.2) * mm, "mid": v(23.1, -27.9) * mm, "end": v(22.5, -28.08) * mm});
            skLineSegment(sketch, "E13.22.5", {"start": v(24.39, -29.07) * mm, "end": v(23.65, -28.2) * mm});
            skArc(sketch, "E13.22.6", {"start": v(24.39, -29.07) * mm, "mid": v(24.5, -29.18) * mm, "end": v(24.64, -29.26) * mm});
            skArc(sketch, "E13.22.7", {"start": v(27.29, -29.54) * mm, "mid": v(27.51, -29.18) * mm, "end": v(27.53, -28.75) * mm});
            skArc(sketch, "E13.22.8", {"start": v(26.24, -29.94) * mm, "mid": v(26.67, -29.95) * mm, "end": v(27.05, -29.76) * mm});
            skArc(sketch, "E13.22.9", {"start": v(24.64, -29.26) * mm, "mid": v(25.42, -29.64) * mm, "end": v(26.24, -29.94) * mm});
            skLineSegment(sketch, "E13.22.10", {"start": v(27.05, -29.76) * mm, "end": v(27.17, -29.65) * mm});
            skLineSegment(sketch, "E13.22.11", {"start": v(27.29, -29.54) * mm, "end": v(27.17, -29.65) * mm});
            skArc(sketch, "E13.23.0", {"start": v(29.93, -19.97) * mm, "mid": v(29.8, -20.58) * mm, "end": v(30.14, -21.1) * mm});
            skLineSegment(sketch, "E13.23.1", {"start": v(31.08, -21.76) * mm, "end": v(30.14, -21.1) * mm});
            skArc(sketch, "E13.23.2", {"start": v(31.3, -22) * mm, "mid": v(31.2, -21.87) * mm, "end": v(31.08, -21.76) * mm});
            skArc(sketch, "E13.23.3", {"start": v(31.3, -22) * mm, "mid": v(31.74, -22.74) * mm, "end": v(32.1, -23.53) * mm});
            skArc(sketch, "E13.23.4", {"start": v(28.2, -23.65) * mm, "mid": v(27.6, -23.46) * mm, "end": v(27.04, -23.74) * mm});
            skLineSegment(sketch, "E13.23.5", {"start": v(29.07, -24.39) * mm, "end": v(28.2, -23.65) * mm});
            skArc(sketch, "E13.23.6", {"start": v(29.07, -24.39) * mm, "mid": v(29.2, -24.48) * mm, "end": v(29.34, -24.54) * mm});
            skArc(sketch, "E13.23.7", {"start": v(32, -24.35) * mm, "mid": v(32.16, -23.96) * mm, "end": v(32.1, -23.53) * mm});
            skArc(sketch, "E13.23.8", {"start": v(31.04, -24.92) * mm, "mid": v(31.47, -24.87) * mm, "end": v(31.8, -24.6) * mm});
            skArc(sketch, "E13.23.9", {"start": v(29.34, -24.54) * mm, "mid": v(30.18, -24.77) * mm, "end": v(31.04, -24.92) * mm});
            skLineSegment(sketch, "E13.23.10", {"start": v(31.8, -24.6) * mm, "end": v(31.9, -24.48) * mm});
            skLineSegment(sketch, "E13.23.11", {"start": v(32, -24.35) * mm, "end": v(31.9, -24.48) * mm});
            skArc(sketch, "E13.24.0", {"start": v(32.94, -14.47) * mm, "mid": v(32.93, -15.1) * mm, "end": v(33.35, -15.55) * mm});
            skLineSegment(sketch, "E13.24.1", {"start": v(34.39, -16.04) * mm, "end": v(33.35, -15.55) * mm});
            skArc(sketch, "E13.24.2", {"start": v(34.64, -16.22) * mm, "mid": v(34.52, -16.12) * mm, "end": v(34.39, -16.04) * mm});
            skArc(sketch, "E13.24.3", {"start": v(34.64, -16.22) * mm, "mid": v(35.2, -16.89) * mm, "end": v(35.7, -17.6) * mm});
            skArc(sketch, "E13.24.4", {"start": v(31.87, -18.4) * mm, "mid": v(31.25, -18.31) * mm, "end": v(30.75, -18.69) * mm});
            skLineSegment(sketch, "E13.24.5", {"start": v(32.86, -18.97) * mm, "end": v(31.87, -18.4) * mm});
            skArc(sketch, "E13.24.6", {"start": v(32.86, -18.97) * mm, "mid": v(33, -19.04) * mm, "end": v(33.16, -19.07) * mm});
            skArc(sketch, "E13.24.7", {"start": v(35.74, -18.42) * mm, "mid": v(35.83, -18) * mm, "end": v(35.7, -17.6) * mm});
            skArc(sketch, "E13.24.8", {"start": v(34.9, -19.15) * mm, "mid": v(35.3, -19.03) * mm, "end": v(35.6, -18.71) * mm});
            skArc(sketch, "E13.24.9", {"start": v(33.16, -19.07) * mm, "mid": v(34.03, -19.15) * mm, "end": v(34.9, -19.15) * mm});
            skLineSegment(sketch, "E13.24.10", {"start": v(35.6, -18.71) * mm, "end": v(35.67, -18.57) * mm});
            skLineSegment(sketch, "E13.24.11", {"start": v(35.74, -18.42) * mm, "end": v(35.67, -18.57) * mm});
            skArc(sketch, "E13.25.0", {"start": v(34.96, -8.53) * mm, "mid": v(35.05, -9.15) * mm, "end": v(35.55, -9.52) * mm});
            skLineSegment(sketch, "E13.25.1", {"start": v(36.65, -9.82) * mm, "end": v(35.55, -9.52) * mm});
            skArc(sketch, "E13.25.2", {"start": v(36.93, -9.96) * mm, "mid": v(36.8, -9.88) * mm, "end": v(36.65, -9.82) * mm});
            skArc(sketch, "E13.25.3", {"start": v(36.93, -9.96) * mm, "mid": v(37.6, -10.52) * mm, "end": v(38.22, -11.13) * mm});
            skArc(sketch, "E13.25.4", {"start": v(34.58, -12.59) * mm, "mid": v(33.96, -12.6) * mm, "end": v(33.53, -13.06) * mm});
            skLineSegment(sketch, "E13.25.5", {"start": v(35.65, -12.98) * mm, "end": v(34.58, -12.59) * mm});
            skArc(sketch, "E13.25.6", {"start": v(35.65, -12.98) * mm, "mid": v(35.8, -13.02) * mm, "end": v(35.97, -13.03) * mm});
            skArc(sketch, "E13.25.7", {"start": v(38.4, -11.94) * mm, "mid": v(38.42, -11.51) * mm, "end": v(38.22, -11.13) * mm});
            skArc(sketch, "E13.25.8", {"start": v(37.7, -12.8) * mm, "mid": v(38.07, -12.6) * mm, "end": v(38.3, -12.25) * mm});
            skArc(sketch, "E13.25.9", {"start": v(35.97, -13.03) * mm, "mid": v(36.84, -12.95) * mm, "end": v(37.7, -12.8) * mm});
            skLineSegment(sketch, "E13.25.10", {"start": v(38.3, -12.25) * mm, "end": v(38.35, -12.1) * mm});
            skLineSegment(sketch, "E13.25.11", {"start": v(38.4, -11.94) * mm, "end": v(38.35, -12.1) * mm});
            skArc(sketch, "E13.26.0", {"start": v(35.9, -2.33) * mm, "mid": v(36.1, -2.92) * mm, "end": v(36.66, -3.2) * mm});
            skLineSegment(sketch, "E13.26.1", {"start": v(37.8, -3.3) * mm, "end": v(36.66, -3.2) * mm});
            skArc(sketch, "E13.26.2", {"start": v(38.1, -3.4) * mm, "mid": v(37.95, -3.34) * mm, "end": v(37.8, -3.3) * mm});
            skArc(sketch, "E13.26.3", {"start": v(38.1, -3.4) * mm, "mid": v(38.86, -3.83) * mm, "end": v(39.57, -4.33) * mm});
            skArc(sketch, "E13.26.4", {"start": v(36.24, -6.4) * mm, "mid": v(35.63, -6.52) * mm, "end": v(35.29, -7.04) * mm});
            skLineSegment(sketch, "E13.26.5", {"start": v(37.37, -6.59) * mm, "end": v(36.24, -6.4) * mm});
            skArc(sketch, "E13.26.6", {"start": v(37.37, -6.59) * mm, "mid": v(37.52, -6.6) * mm, "end": v(37.68, -6.58) * mm});
            skArc(sketch, "E13.26.7", {"start": v(39.89, -5.09) * mm, "mid": v(39.83, -4.67) * mm, "end": v(39.57, -4.33) * mm});
            skArc(sketch, "E13.26.8", {"start": v(39.35, -6.06) * mm, "mid": v(39.68, -5.8) * mm, "end": v(39.85, -5.4) * mm});
            skArc(sketch, "E13.26.9", {"start": v(37.68, -6.58) * mm, "mid": v(38.53, -6.36) * mm, "end": v(39.35, -6.06) * mm});
            skLineSegment(sketch, "E13.26.10", {"start": v(39.85, -5.4) * mm, "end": v(39.87, -5.25) * mm});
            skLineSegment(sketch, "E13.26.11", {"start": v(39.89, -5.09) * mm, "end": v(39.87, -5.25) * mm});
            skArc(sketch, "E13.27.0", {"start": v(35.77, 3.94) * mm, "mid": v(36.06, 3.4) * mm, "end": v(36.66, 3.2) * mm});
            skLineSegment(sketch, "E13.27.1", {"start": v(37.8, 3.3) * mm, "end": v(36.66, 3.2) * mm});
            skArc(sketch, "E13.27.2", {"start": v(38.11, 3.27) * mm, "mid": v(37.96, 3.3) * mm, "end": v(37.8, 3.3) * mm});
            skArc(sketch, "E13.27.3", {"start": v(38.11, 3.27) * mm, "mid": v(38.93, 2.98) * mm, "end": v(39.72, 2.61) * mm});
            skArc(sketch, "E13.27.4", {"start": v(36.8, 0) * mm, "mid": v(36.22, -0.24) * mm, "end": v(35.97, -0.8) * mm});
            skLineSegment(sketch, "E13.27.5", {"start": v(37.94, 0) * mm, "end": v(36.8, 0) * mm});
            skArc(sketch, "E13.27.6", {"start": v(37.94, 0) * mm, "mid": v(38.1, 0.02) * mm, "end": v(38.25, 0.06) * mm});
            skArc(sketch, "E13.27.7", {"start": v(40.17, 1.91) * mm, "mid": v(40.04, 2.32) * mm, "end": v(39.72, 2.61) * mm});
            skArc(sketch, "E13.27.8", {"start": v(39.8, 0.86) * mm, "mid": v(40.09, 1.18) * mm, "end": v(40.18, 1.6) * mm});
            skArc(sketch, "E13.27.9", {"start": v(38.25, 0.06) * mm, "mid": v(39.05, 0.43) * mm, "end": v(39.8, 0.86) * mm});
            skLineSegment(sketch, "E13.27.10", {"start": v(40.18, 1.6) * mm, "end": v(40.17, 1.75) * mm});
            skLineSegment(sketch, "E13.27.11", {"start": v(40.17, 1.91) * mm, "end": v(40.17, 1.75) * mm});
            skArc(sketch, "E13.28.0", {"start": v(34.54, 10.1) * mm, "mid": v(34.93, 9.6) * mm, "end": v(35.55, 9.52) * mm});
            skLineSegment(sketch, "E13.28.1", {"start": v(36.65, 9.82) * mm, "end": v(35.55, 9.52) * mm});
            skArc(sketch, "E13.28.2", {"start": v(36.97, 9.84) * mm, "mid": v(36.8, 9.85) * mm, "end": v(36.65, 9.82) * mm});
            skArc(sketch, "E13.28.3", {"start": v(36.97, 9.84) * mm, "mid": v(37.83, 9.7) * mm, "end": v(38.67, 9.47) * mm});
            skArc(sketch, "E13.28.4", {"start": v(36.24, 6.4) * mm, "mid": v(35.71, 6.06) * mm, "end": v(35.57, 5.45) * mm});
            skLineSegment(sketch, "E13.28.5", {"start": v(37.37, 6.59) * mm, "end": v(36.24, 6.4) * mm});
            skArc(sketch, "E13.28.6", {"start": v(37.37, 6.59) * mm, "mid": v(37.52, 6.63) * mm, "end": v(37.66, 6.7) * mm});
            skArc(sketch, "E13.28.7", {"start": v(39.22, 8.86) * mm, "mid": v(39.03, 9.24) * mm, "end": v(38.67, 9.47) * mm});
            skArc(sketch, "E13.28.8", {"start": v(39.05, 7.76) * mm, "mid": v(39.27, 8.12) * mm, "end": v(39.3, 8.55) * mm});
            skArc(sketch, "E13.28.9", {"start": v(37.66, 6.7) * mm, "mid": v(38.38, 7.2) * mm, "end": v(39.05, 7.76) * mm});
            skLineSegment(sketch, "E13.28.10", {"start": v(39.3, 8.55) * mm, "end": v(39.26, 8.7) * mm});
            skLineSegment(sketch, "E13.28.11", {"start": v(39.22, 8.86) * mm, "end": v(39.26, 8.7) * mm});
            skArc(sketch, "E13.29.0", {"start": v(32.26, 15.93) * mm, "mid": v(32.73, 15.52) * mm, "end": v(33.35, 15.55) * mm});
            skLineSegment(sketch, "E13.29.1", {"start": v(34.39, 16.04) * mm, "end": v(33.35, 15.55) * mm});
            skArc(sketch, "E13.29.2", {"start": v(34.7, 16.11) * mm, "mid": v(34.54, 16.09) * mm, "end": v(34.39, 16.04) * mm});
            skArc(sketch, "E13.29.3", {"start": v(34.7, 16.11) * mm, "mid": v(35.57, 16.12) * mm, "end": v(36.44, 16.04) * mm});
            skArc(sketch, "E13.29.4", {"start": v(34.58, 12.59) * mm, "mid": v(34.12, 12.17) * mm, "end": v(34.08, 11.55) * mm});
            skLineSegment(sketch, "E13.29.5", {"start": v(35.65, 12.98) * mm, "end": v(34.58, 12.59) * mm});
            skArc(sketch, "E13.29.6", {"start": v(35.65, 12.98) * mm, "mid": v(35.8, 13.05) * mm, "end": v(35.93, 13.14) * mm});
            skArc(sketch, "E13.29.7", {"start": v(37.09, 15.54) * mm, "mid": v(36.83, 15.88) * mm, "end": v(36.44, 16.04) * mm});
            skArc(sketch, "E13.29.8", {"start": v(37.1, 14.42) * mm, "mid": v(37.27, 14.82) * mm, "end": v(37.21, 15.24) * mm});
            skArc(sketch, "E13.29.9", {"start": v(35.93, 13.14) * mm, "mid": v(36.54, 13.75) * mm, "end": v(37.1, 14.42) * mm});
            skLineSegment(sketch, "E13.29.10", {"start": v(37.21, 15.24) * mm, "end": v(37.15, 15.39) * mm});
            skLineSegment(sketch, "E13.29.11", {"start": v(37.09, 15.54) * mm, "end": v(37.15, 15.39) * mm});
            skArc(sketch, "E13.30.0", {"start": v(29, 21.3) * mm, "mid": v(29.54, 20.97) * mm, "end": v(30.14, 21.1) * mm});
            skLineSegment(sketch, "E13.30.1", {"start": v(31.08, 21.76) * mm, "end": v(30.14, 21.1) * mm});
            skArc(sketch, "E13.30.2", {"start": v(31.37, 21.9) * mm, "mid": v(31.22, 21.84) * mm, "end": v(31.08, 21.76) * mm});
            skArc(sketch, "E13.30.3", {"start": v(31.37, 21.9) * mm, "mid": v(32.23, 22.05) * mm, "end": v(33.1, 22.12) * mm});
            skArc(sketch, "E13.30.4", {"start": v(31.87, 18.4) * mm, "mid": v(31.49, 17.9) * mm, "end": v(31.56, 17.29) * mm});
            skLineSegment(sketch, "E13.30.5", {"start": v(32.86, 18.97) * mm, "end": v(31.87, 18.4) * mm});
            skArc(sketch, "E13.30.6", {"start": v(32.86, 18.97) * mm, "mid": v(32.99, 19.06) * mm, "end": v(33.1, 19.18) * mm});
            skArc(sketch, "E13.30.7", {"start": v(33.83, 21.74) * mm, "mid": v(33.51, 22.03) * mm, "end": v(33.1, 22.12) * mm});
            skArc(sketch, "E13.30.8", {"start": v(34.04, 20.65) * mm, "mid": v(34.13, 21.06) * mm, "end": v(34, 21.47) * mm});
            skArc(sketch, "E13.30.9", {"start": v(33.1, 19.18) * mm, "mid": v(33.6, 19.9) * mm, "end": v(34.04, 20.65) * mm});
            skLineSegment(sketch, "E13.30.10", {"start": v(34, 21.47) * mm, "end": v(33.91, 21.6) * mm});
            skLineSegment(sketch, "E13.30.11", {"start": v(33.83, 21.74) * mm, "end": v(33.91, 21.6) * mm});
            skArc(sketch, "E13.31.0", {"start": v(24.87, 26) * mm, "mid": v(25.45, 25.78) * mm, "end": v(26.02, 26.02) * mm});
            skLineSegment(sketch, "E13.31.1", {"start": v(26.83, 26.83) * mm, "end": v(26.02, 26.02) * mm});
            skArc(sketch, "E13.31.2", {"start": v(27.1, 27) * mm, "mid": v(26.95, 26.93) * mm, "end": v(26.83, 26.83) * mm});
            skArc(sketch, "E13.31.3", {"start": v(27.1, 27) * mm, "mid": v(27.91, 27.3) * mm, "end": v(28.75, 27.53) * mm});
            skArc(sketch, "E13.31.4", {"start": v(28.2, 23.65) * mm, "mid": v(27.9, 23.1) * mm, "end": v(28.08, 22.5) * mm});
            skLineSegment(sketch, "E13.31.5", {"start": v(29.07, 24.39) * mm, "end": v(28.2, 23.65) * mm});
            skArc(sketch, "E13.31.6", {"start": v(29.07, 24.39) * mm, "mid": v(29.18, 24.5) * mm, "end": v(29.26, 24.64) * mm});
            skArc(sketch, "E13.31.7", {"start": v(29.54, 27.29) * mm, "mid": v(29.18, 27.51) * mm, "end": v(28.75, 27.53) * mm});
            skArc(sketch, "E13.31.8", {"start": v(29.94, 26.24) * mm, "mid": v(29.95, 26.67) * mm, "end": v(29.76, 27.05) * mm});
            skArc(sketch, "E13.31.9", {"start": v(29.26, 24.64) * mm, "mid": v(29.64, 25.42) * mm, "end": v(29.94, 26.24) * mm});
            skLineSegment(sketch, "E13.31.10", {"start": v(29.76, 27.05) * mm, "end": v(29.65, 27.17) * mm});
            skLineSegment(sketch, "E13.31.11", {"start": v(29.54, 27.29) * mm, "end": v(29.65, 27.17) * mm});
            skArc(sketch, "E13.32.0", {"start": v(19.97, 29.93) * mm, "mid": v(20.58, 29.8) * mm, "end": v(21.1, 30.14) * mm});
            skLineSegment(sketch, "E13.32.1", {"start": v(21.76, 31.08) * mm, "end": v(21.1, 30.14) * mm});
            skArc(sketch, "E13.32.2", {"start": v(22, 31.3) * mm, "mid": v(21.87, 31.2) * mm, "end": v(21.76, 31.08) * mm});
            skArc(sketch, "E13.32.3", {"start": v(22, 31.3) * mm, "mid": v(22.74, 31.74) * mm, "end": v(23.53, 32.1) * mm});
            skArc(sketch, "E13.32.4", {"start": v(23.65, 28.2) * mm, "mid": v(23.46, 27.6) * mm, "end": v(23.74, 27.04) * mm});
            skLineSegment(sketch, "E13.32.5", {"start": v(24.39, 29.07) * mm, "end": v(23.65, 28.2) * mm});
            skArc(sketch, "E13.32.6", {"start": v(24.39, 29.07) * mm, "mid": v(24.48, 29.2) * mm, "end": v(24.54, 29.34) * mm});
            skArc(sketch, "E13.32.7", {"start": v(24.35, 32) * mm, "mid": v(23.96, 32.16) * mm, "end": v(23.53, 32.1) * mm});
            skArc(sketch, "E13.32.8", {"start": v(24.92, 31.04) * mm, "mid": v(24.87, 31.47) * mm, "end": v(24.6, 31.8) * mm});
            skArc(sketch, "E13.32.9", {"start": v(24.54, 29.34) * mm, "mid": v(24.77, 30.18) * mm, "end": v(24.92, 31.04) * mm});
            skLineSegment(sketch, "E13.32.10", {"start": v(24.6, 31.8) * mm, "end": v(24.48, 31.9) * mm});
            skLineSegment(sketch, "E13.32.11", {"start": v(24.35, 32) * mm, "end": v(24.48, 31.9) * mm});
            skArc(sketch, "E13.33.0", {"start": v(14.47, 32.94) * mm, "mid": v(15.1, 32.93) * mm, "end": v(15.55, 33.35) * mm});
            skLineSegment(sketch, "E13.33.1", {"start": v(16.04, 34.39) * mm, "end": v(15.55, 33.35) * mm});
            skArc(sketch, "E13.33.2", {"start": v(16.22, 34.64) * mm, "mid": v(16.12, 34.52) * mm, "end": v(16.04, 34.39) * mm});
            skArc(sketch, "E13.33.3", {"start": v(16.22, 34.64) * mm, "mid": v(16.89, 35.2) * mm, "end": v(17.6, 35.7) * mm});
            skArc(sketch, "E13.33.4", {"start": v(18.4, 31.87) * mm, "mid": v(18.31, 31.25) * mm, "end": v(18.69, 30.75) * mm});
            skLineSegment(sketch, "E13.33.5", {"start": v(18.97, 32.86) * mm, "end": v(18.4, 31.87) * mm});
            skArc(sketch, "E13.33.6", {"start": v(18.97, 32.86) * mm, "mid": v(19.04, 33) * mm, "end": v(19.07, 33.16) * mm});
            skArc(sketch, "E13.33.7", {"start": v(18.42, 35.74) * mm, "mid": v(18, 35.83) * mm, "end": v(17.6, 35.7) * mm});
            skArc(sketch, "E13.33.8", {"start": v(19.15, 34.9) * mm, "mid": v(19.03, 35.3) * mm, "end": v(18.71, 35.6) * mm});
            skArc(sketch, "E13.33.9", {"start": v(19.07, 33.16) * mm, "mid": v(19.15, 34.03) * mm, "end": v(19.15, 34.9) * mm});
            skLineSegment(sketch, "E13.33.10", {"start": v(18.71, 35.6) * mm, "end": v(18.57, 35.67) * mm});
            skLineSegment(sketch, "E13.33.11", {"start": v(18.42, 35.74) * mm, "end": v(18.57, 35.67) * mm});
            skArc(sketch, "E13.34.0", {"start": v(8.53, 34.96) * mm, "mid": v(9.15, 35.05) * mm, "end": v(9.52, 35.55) * mm});
            skLineSegment(sketch, "E13.34.1", {"start": v(9.82, 36.65) * mm, "end": v(9.52, 35.55) * mm});
            skArc(sketch, "E13.34.2", {"start": v(9.96, 36.93) * mm, "mid": v(9.88, 36.8) * mm, "end": v(9.82, 36.65) * mm});
            skArc(sketch, "E13.34.3", {"start": v(9.96, 36.93) * mm, "mid": v(10.52, 37.6) * mm, "end": v(11.13, 38.22) * mm});
            skArc(sketch, "E13.34.4", {"start": v(12.59, 34.58) * mm, "mid": v(12.6, 33.96) * mm, "end": v(13.06, 33.53) * mm});
            skLineSegment(sketch, "E13.34.5", {"start": v(12.98, 35.65) * mm, "end": v(12.59, 34.58) * mm});
            skArc(sketch, "E13.34.6", {"start": v(12.98, 35.65) * mm, "mid": v(13.02, 35.8) * mm, "end": v(13.03, 35.97) * mm});
            skArc(sketch, "E13.34.7", {"start": v(11.94, 38.4) * mm, "mid": v(11.51, 38.42) * mm, "end": v(11.13, 38.22) * mm});
            skArc(sketch, "E13.34.8", {"start": v(12.8, 37.7) * mm, "mid": v(12.6, 38.07) * mm, "end": v(12.25, 38.3) * mm});
            skArc(sketch, "E13.34.9", {"start": v(13.03, 35.97) * mm, "mid": v(12.95, 36.84) * mm, "end": v(12.8, 37.7) * mm});
            skLineSegment(sketch, "E13.34.10", {"start": v(12.25, 38.3) * mm, "end": v(12.1, 38.35) * mm});
            skLineSegment(sketch, "E13.34.11", {"start": v(11.94, 38.4) * mm, "end": v(12.1, 38.35) * mm});
            skArc(sketch, "E13.35.0", {"start": v(2.33, 35.9) * mm, "mid": v(2.92, 36.1) * mm, "end": v(3.2, 36.66) * mm});
            skLineSegment(sketch, "E13.35.1", {"start": v(3.3, 37.8) * mm, "end": v(3.2, 36.66) * mm});
            skArc(sketch, "E13.35.2", {"start": v(3.4, 38.1) * mm, "mid": v(3.34, 37.95) * mm, "end": v(3.3, 37.8) * mm});
            skArc(sketch, "E13.35.3", {"start": v(3.4, 38.1) * mm, "mid": v(3.83, 38.86) * mm, "end": v(4.33, 39.57) * mm});
            skArc(sketch, "E13.35.4", {"start": v(6.4, 36.24) * mm, "mid": v(6.52, 35.63) * mm, "end": v(7.04, 35.29) * mm});
            skLineSegment(sketch, "E13.35.5", {"start": v(6.59, 37.37) * mm, "end": v(6.4, 36.24) * mm});
            skArc(sketch, "E13.35.6", {"start": v(6.59, 37.37) * mm, "mid": v(6.6, 37.52) * mm, "end": v(6.58, 37.68) * mm});
            skArc(sketch, "E13.35.7", {"start": v(5.09, 39.89) * mm, "mid": v(4.67, 39.83) * mm, "end": v(4.33, 39.57) * mm});
            skArc(sketch, "E13.35.8", {"start": v(6.06, 39.35) * mm, "mid": v(5.8, 39.68) * mm, "end": v(5.4, 39.85) * mm});
            skArc(sketch, "E13.35.9", {"start": v(6.58, 37.68) * mm, "mid": v(6.36, 38.53) * mm, "end": v(6.06, 39.35) * mm});
            skLineSegment(sketch, "E13.35.10", {"start": v(5.4, 39.85) * mm, "end": v(5.25, 39.87) * mm});
            skLineSegment(sketch, "E13.35.11", {"start": v(5.09, 39.89) * mm, "end": v(5.25, 39.87) * mm});
            skPoint(sketch, "E13.center", {"position": v(0, 0) * mm});
            skArc(sketch, "E14.trimOffspring", {"start": v(-21.3, 29) * mm, "mid": v(-21.9, 28.55) * mm, "end": v(-22.5, 28.08) * mm});
            skArc(sketch, "E15.trimOffspring", {"start": v(-15.93, 32.26) * mm, "mid": v(-16.62, 31.92) * mm, "end": v(-17.29, 31.56) * mm});
            skArc(sketch, "E16.trimOffspring", {"start": v(-10.1, 34.54) * mm, "mid": v(-10.82, 34.32) * mm, "end": v(-11.55, 34.08) * mm});
            skArc(sketch, "E17.trimOffspring", {"start": v(2.33, 35.9) * mm, "mid": v(1.57, 35.95) * mm, "end": v(0.8, 35.97) * mm});
            skArc(sketch, "E18.trimOffspring", {"start": v(8.53, 34.96) * mm, "mid": v(7.79, 35.13) * mm, "end": v(7.04, 35.29) * mm});
            skArc(sketch, "E19.trimOffspring", {"start": v(14.47, 32.94) * mm, "mid": v(13.77, 33.24) * mm, "end": v(13.06, 33.53) * mm});
            skArc(sketch, "E20.trimOffspring", {"start": v(19.97, 29.93) * mm, "mid": v(19.33, 30.35) * mm, "end": v(18.69, 30.75) * mm});
            skArc(sketch, "E21.trimOffspring", {"start": v(24.87, 26) * mm, "mid": v(24.3, 26.53) * mm, "end": v(23.74, 27.04) * mm});
            skArc(sketch, "E22.trimOffspring", {"start": v(29, 21.3) * mm, "mid": v(28.55, 21.9) * mm, "end": v(28.08, 22.5) * mm});
            skArc(sketch, "E23.trimOffspring", {"start": v(32.26, 15.93) * mm, "mid": v(31.92, 16.62) * mm, "end": v(31.56, 17.29) * mm});
            skArc(sketch, "E24.trimOffspring", {"start": v(34.54, 10.1) * mm, "mid": v(34.32, 10.82) * mm, "end": v(34.08, 11.55) * mm});
            skArc(sketch, "E25.trimOffspring", {"start": v(35.77, 3.94) * mm, "mid": v(35.68, 4.7) * mm, "end": v(35.57, 5.45) * mm});
            skArc(sketch, "E26.trimOffspring", {"start": v(35.9, -2.33) * mm, "mid": v(35.95, -1.57) * mm, "end": v(35.97, -0.8) * mm});
            skArc(sketch, "E27.trimOffspring", {"start": v(34.96, -8.53) * mm, "mid": v(35.13, -7.79) * mm, "end": v(35.29, -7.04) * mm});
            skArc(sketch, "E28.trimOffspring", {"start": v(32.94, -14.47) * mm, "mid": v(33.24, -13.77) * mm, "end": v(33.53, -13.06) * mm});
            skArc(sketch, "E29.trimOffspring", {"start": v(29.93, -19.97) * mm, "mid": v(30.35, -19.33) * mm, "end": v(30.75, -18.69) * mm});
            skArc(sketch, "E30.trimOffspring", {"start": v(26, -24.87) * mm, "mid": v(26.53, -24.3) * mm, "end": v(27.04, -23.74) * mm});
            skArc(sketch, "E31.trimOffspring", {"start": v(21.3, -29) * mm, "mid": v(21.9, -28.55) * mm, "end": v(22.5, -28.08) * mm});
            skArc(sketch, "E32.trimOffspring", {"start": v(15.93, -32.26) * mm, "mid": v(16.62, -31.92) * mm, "end": v(17.29, -31.56) * mm});
            skArc(sketch, "E33.trimOffspring", {"start": v(10.1, -34.54) * mm, "mid": v(10.82, -34.32) * mm, "end": v(11.55, -34.08) * mm});
            skArc(sketch, "E34.trimOffspring", {"start": v(3.94, -35.77) * mm, "mid": v(4.7, -35.68) * mm, "end": v(5.45, -35.57) * mm});
            skArc(sketch, "E35.trimOffspring", {"start": v(-2.33, -35.9) * mm, "mid": v(-1.57, -35.95) * mm, "end": v(-0.8, -35.97) * mm});
            skArc(sketch, "E36.trimOffspring", {"start": v(-8.53, -34.96) * mm, "mid": v(-7.79, -35.13) * mm, "end": v(-7.04, -35.29) * mm});
            skArc(sketch, "E37.trimOffspring", {"start": v(-14.47, -32.94) * mm, "mid": v(-13.77, -33.24) * mm, "end": v(-13.06, -33.53) * mm});
            skArc(sketch, "E38.trimOffspring", {"start": v(-19.97, -29.93) * mm, "mid": v(-19.33, -30.35) * mm, "end": v(-18.69, -30.75) * mm});
            skArc(sketch, "E39.trimOffspring", {"start": v(-24.87, -26) * mm, "mid": v(-24.3, -26.53) * mm, "end": v(-23.74, -27.04) * mm});
            skArc(sketch, "E40.trimOffspring", {"start": v(-29, -21.3) * mm, "mid": v(-28.55, -21.9) * mm, "end": v(-28.08, -22.5) * mm});
            skArc(sketch, "E41.trimOffspring", {"start": v(-32.26, -15.93) * mm, "mid": v(-31.92, -16.62) * mm, "end": v(-31.56, -17.29) * mm});
            skArc(sketch, "E42.trimOffspring", {"start": v(-34.54, -10.1) * mm, "mid": v(-34.32, -10.82) * mm, "end": v(-34.08, -11.55) * mm});
            skArc(sketch, "E43.trimOffspring", {"start": v(-35.77, -3.94) * mm, "mid": v(-35.68, -4.7) * mm, "end": v(-35.57, -5.45) * mm});
            skArc(sketch, "E44.trimOffspring", {"start": v(-35.9, 2.33) * mm, "mid": v(-35.95, 1.57) * mm, "end": v(-35.97, 0.8) * mm});
            skArc(sketch, "E45.trimOffspring", {"start": v(-34.96, 8.53) * mm, "mid": v(-35.13, 7.79) * mm, "end": v(-35.29, 7.04) * mm});
            skArc(sketch, "E46.trimOffspring", {"start": v(-32.94, 14.47) * mm, "mid": v(-33.24, 13.77) * mm, "end": v(-33.53, 13.06) * mm});
            skArc(sketch, "E47.trimOffspring", {"start": v(-29.93, 19.97) * mm, "mid": v(-30.35, 19.33) * mm, "end": v(-30.75, 18.69) * mm});
            skArc(sketch, "E48.trimOffspring", {"start": v(-26, 24.87) * mm, "mid": v(-26.53, 24.3) * mm, "end": v(-27.04, 23.74) * mm});
            skLineSegment(sketch, "E49", {"start": v(-3.94, 35.77) * mm, "end": v(-5.45, 35.57) * mm});
            skSolve(sketch);
        }
        {
            var Q0;
            Q0=makeQuery(id+"F0.imprint","IMPRINT",FACE,{"disambiguationData":[TD([[makeQuery(id+"F0.imprint","IMPRINT",EDGE,{"derivedFrom":sQuery(id+"F0.wireOp",EDGE,"E1.trimOffspring")}),1.0]])]});
            extrude(context, id + "F1", {"entities" : qUnion([Q0]), "depth" : 12.7 * mm});
        }
        {
            var Q0;
            Q0=makeQuery(id+"F1.opExtrude","CAP_FACE",FACE,{"disambiguationData":[OSD([sQuery(id+"F0.wireOp",EDGE,"E1.trimOffspring"),sQuery(id+"F0.wireOp",EDGE,"E2"),sQuery(id+"F0.wireOp",EDGE,"E3"),sQuery(id+"F0.wireOp",EDGE,"E4.MirrorCS"),sQuery(id+"F0.wireOp",EDGE,"E5.MirrorCS"),sQuery(id+"F0.wireOp",EDGE,"E6.MirrorCS"),sQuery(id+"F0.wireOp",EDGE,"E7.filletArc"),sQuery(id+"F0.wireOp",EDGE,"E8.filletArc"),sQuery(id+"F0.wireOp",EDGE,"E9.filletArc"),sQuery(id+"F0.wireOp",EDGE,"E10.filletArc"),sQuery(id+"F0.wireOp",EDGE,"E11.filletArc"),sQuery(id+"F0.wireOp",EDGE,"E12.filletArc"),sQuery(id+"F0.wireOp",EDGE,"E13.1.0"),sQuery(id+"F0.wireOp",EDGE,"E13.1.1"),sQuery(id+"F0.wireOp",EDGE,"E13.1.2"),sQuery(id+"F0.wireOp",EDGE,"E13.1.3"),sQuery(id+"F0.wireOp",EDGE,"E13.1.4"),sQuery(id+"F0.wireOp",EDGE,"E13.1.5"),sQuery(id+"F0.wireOp",EDGE,"E13.1.6"),sQuery(id+"F0.wireOp",EDGE,"E13.1.7"),sQuery(id+"F0.wireOp",EDGE,"E13.1.8"),sQuery(id+"F0.wireOp",EDGE,"E13.1.9"),sQuery(id+"F0.wireOp",EDGE,"E13.1.10"),sQuery(id+"F0.wireOp",EDGE,"E13.1.11"),sQuery(id+"F0.wireOp",EDGE,"E13.2.0"),sQuery(id+"F0.wireOp",EDGE,"E13.2.1"),sQuery(id+"F0.wireOp",EDGE,"E13.2.2"),sQuery(id+"F0.wireOp",EDGE,"E13.2.3"),sQuery(id+"F0.wireOp",EDGE,"E13.2.4"),sQuery(id+"F0.wireOp",EDGE,"E13.2.5"),sQuery(id+"F0.wireOp",EDGE,"E13.2.6"),sQuery(id+"F0.wireOp",EDGE,"E13.2.7"),sQuery(id+"F0.wireOp",EDGE,"E13.2.8"),sQuery(id+"F0.wireOp",EDGE,"E13.2.9"),sQuery(id+"F0.wireOp",EDGE,"E13.2.10"),sQuery(id+"F0.wireOp",EDGE,"E13.2.11"),sQuery(id+"F0.wireOp",EDGE,"E13.3.0"),sQuery(id+"F0.wireOp",EDGE,"E13.3.1"),sQuery(id+"F0.wireOp",EDGE,"E13.3.2"),sQuery(id+"F0.wireOp",EDGE,"E13.3.3"),sQuery(id+"F0.wireOp",EDGE,"E13.3.4"),sQuery(id+"F0.wireOp",EDGE,"E13.3.5"),sQuery(id+"F0.wireOp",EDGE,"E13.3.6"),sQuery(id+"F0.wireOp",EDGE,"E13.3.7"),sQuery(id+"F0.wireOp",EDGE,"E13.3.8"),sQuery(id+"F0.wireOp",EDGE,"E13.3.9"),sQuery(id+"F0.wireOp",EDGE,"E13.3.10"),sQuery(id+"F0.wireOp",EDGE,"E13.3.11"),sQuery(id+"F0.wireOp",EDGE,"E13.4.0"),sQuery(id+"F0.wireOp",EDGE,"E13.4.1"),sQuery(id+"F0.wireOp",EDGE,"E13.4.2"),sQuery(id+"F0.wireOp",EDGE,"E13.4.3"),sQuery(id+"F0.wireOp",EDGE,"E13.4.4"),sQuery(id+"F0.wireOp",EDGE,"E13.4.5"),sQuery(id+"F0.wireOp",EDGE,"E13.4.6"),sQuery(id+"F0.wireOp",EDGE,"E13.4.7"),sQuery(id+"F0.wireOp",EDGE,"E13.4.8"),sQuery(id+"F0.wireOp",EDGE,"E13.4.9"),sQuery(id+"F0.wireOp",EDGE,"E13.4.10"),sQuery(id+"F0.wireOp",EDGE,"E13.4.11"),sQuery(id+"F0.wireOp",EDGE,"E13.5.0"),sQuery(id+"F0.wireOp",EDGE,"E13.5.1"),sQuery(id+"F0.wireOp",EDGE,"E13.5.2"),sQuery(id+"F0.wireOp",EDGE,"E13.5.3"),sQuery(id+"F0.wireOp",EDGE,"E13.5.4"),sQuery(id+"F0.wireOp",EDGE,"E13.5.5"),sQuery(id+"F0.wireOp",EDGE,"E13.5.6"),sQuery(id+"F0.wireOp",EDGE,"E13.5.7"),sQuery(id+"F0.wireOp",EDGE,"E13.5.8"),sQuery(id+"F0.wireOp",EDGE,"E13.5.9"),sQuery(id+"F0.wireOp",EDGE,"E13.5.10"),sQuery(id+"F0.wireOp",EDGE,"E13.5.11"),sQuery(id+"F0.wireOp",EDGE,"E13.6.0"),sQuery(id+"F0.wireOp",EDGE,"E13.6.1"),sQuery(id+"F0.wireOp",EDGE,"E13.6.2"),sQuery(id+"F0.wireOp",EDGE,"E13.6.3"),sQuery(id+"F0.wireOp",EDGE,"E13.6.4"),sQuery(id+"F0.wireOp",EDGE,"E13.6.5"),sQuery(id+"F0.wireOp",EDGE,"E13.6.6"),sQuery(id+"F0.wireOp",EDGE,"E13.6.7"),sQuery(id+"F0.wireOp",EDGE,"E13.6.8"),sQuery(id+"F0.wireOp",EDGE,"E13.6.9"),sQuery(id+"F0.wireOp",EDGE,"E13.6.10"),sQuery(id+"F0.wireOp",EDGE,"E13.6.11"),sQuery(id+"F0.wireOp",EDGE,"E13.7.0"),sQuery(id+"F0.wireOp",EDGE,"E13.7.1"),sQuery(id+"F0.wireOp",EDGE,"E13.7.2"),sQuery(id+"F0.wireOp",EDGE,"E13.7.3"),sQuery(id+"F0.wireOp",EDGE,"E13.7.4"),sQuery(id+"F0.wireOp",EDGE,"E13.7.5"),sQuery(id+"F0.wireOp",EDGE,"E13.7.6"),sQuery(id+"F0.wireOp",EDGE,"E13.7.7"),sQuery(id+"F0.wireOp",EDGE,"E13.7.8"),sQuery(id+"F0.wireOp",EDGE,"E13.7.9"),sQuery(id+"F0.wireOp",EDGE,"E13.7.10"),sQuery(id+"F0.wireOp",EDGE,"E13.7.11"),sQuery(id+"F0.wireOp",EDGE,"E13.8.0"),sQuery(id+"F0.wireOp",EDGE,"E13.8.1"),sQuery(id+"F0.wireOp",EDGE,"E13.8.2"),sQuery(id+"F0.wireOp",EDGE,"E13.8.3"),sQuery(id+"F0.wireOp",EDGE,"E13.8.4"),sQuery(id+"F0.wireOp",EDGE,"E13.8.5"),sQuery(id+"F0.wireOp",EDGE,"E13.8.6"),sQuery(id+"F0.wireOp",EDGE,"E13.8.7"),sQuery(id+"F0.wireOp",EDGE,"E13.8.8"),sQuery(id+"F0.wireOp",EDGE,"E13.8.9"),sQuery(id+"F0.wireOp",EDGE,"E13.8.10"),sQuery(id+"F0.wireOp",EDGE,"E13.8.11"),sQuery(id+"F0.wireOp",EDGE,"E13.9.0"),sQuery(id+"F0.wireOp",EDGE,"E13.9.1"),sQuery(id+"F0.wireOp",EDGE,"E13.9.2"),sQuery(id+"F0.wireOp",EDGE,"E13.9.3"),sQuery(id+"F0.wireOp",EDGE,"E13.9.4"),sQuery(id+"F0.wireOp",EDGE,"E13.9.5"),sQuery(id+"F0.wireOp",EDGE,"E13.9.6"),sQuery(id+"F0.wireOp",EDGE,"E13.9.7"),sQuery(id+"F0.wireOp",EDGE,"E13.9.8"),sQuery(id+"F0.wireOp",EDGE,"E13.9.9"),sQuery(id+"F0.wireOp",EDGE,"E13.9.10"),sQuery(id+"F0.wireOp",EDGE,"E13.9.11"),sQuery(id+"F0.wireOp",EDGE,"E13.10.0"),sQuery(id+"F0.wireOp",EDGE,"E13.10.1"),sQuery(id+"F0.wireOp",EDGE,"E13.10.2"),sQuery(id+"F0.wireOp",EDGE,"E13.10.3"),sQuery(id+"F0.wireOp",EDGE,"E13.10.4"),sQuery(id+"F0.wireOp",EDGE,"E13.10.5"),sQuery(id+"F0.wireOp",EDGE,"E13.10.6"),sQuery(id+"F0.wireOp",EDGE,"E13.10.7"),sQuery(id+"F0.wireOp",EDGE,"E13.10.8"),sQuery(id+"F0.wireOp",EDGE,"E13.10.9"),sQuery(id+"F0.wireOp",EDGE,"E13.10.10"),sQuery(id+"F0.wireOp",EDGE,"E13.10.11"),sQuery(id+"F0.wireOp",EDGE,"E13.11.0"),sQuery(id+"F0.wireOp",EDGE,"E13.11.1"),sQuery(id+"F0.wireOp",EDGE,"E13.11.2"),sQuery(id+"F0.wireOp",EDGE,"E13.11.3"),sQuery(id+"F0.wireOp",EDGE,"E13.11.4"),sQuery(id+"F0.wireOp",EDGE,"E13.11.5"),sQuery(id+"F0.wireOp",EDGE,"E13.11.6"),sQuery(id+"F0.wireOp",EDGE,"E13.11.7"),sQuery(id+"F0.wireOp",EDGE,"E13.11.8"),sQuery(id+"F0.wireOp",EDGE,"E13.11.9"),sQuery(id+"F0.wireOp",EDGE,"E13.11.10"),sQuery(id+"F0.wireOp",EDGE,"E13.11.11"),sQuery(id+"F0.wireOp",EDGE,"E13.12.0"),sQuery(id+"F0.wireOp",EDGE,"E13.12.1"),sQuery(id+"F0.wireOp",EDGE,"E13.12.2"),sQuery(id+"F0.wireOp",EDGE,"E13.12.3"),sQuery(id+"F0.wireOp",EDGE,"E13.12.4"),sQuery(id+"F0.wireOp",EDGE,"E13.12.5"),sQuery(id+"F0.wireOp",EDGE,"E13.12.6"),sQuery(id+"F0.wireOp",EDGE,"E13.12.7"),sQuery(id+"F0.wireOp",EDGE,"E13.12.8"),sQuery(id+"F0.wireOp",EDGE,"E13.12.9"),sQuery(id+"F0.wireOp",EDGE,"E13.12.10"),sQuery(id+"F0.wireOp",EDGE,"E13.12.11"),sQuery(id+"F0.wireOp",EDGE,"E13.13.0"),sQuery(id+"F0.wireOp",EDGE,"E13.13.1"),sQuery(id+"F0.wireOp",EDGE,"E13.13.2"),sQuery(id+"F0.wireOp",EDGE,"E13.13.3"),sQuery(id+"F0.wireOp",EDGE,"E13.13.4"),sQuery(id+"F0.wireOp",EDGE,"E13.13.5"),sQuery(id+"F0.wireOp",EDGE,"E13.13.6"),sQuery(id+"F0.wireOp",EDGE,"E13.13.7"),sQuery(id+"F0.wireOp",EDGE,"E13.13.8"),sQuery(id+"F0.wireOp",EDGE,"E13.13.9"),sQuery(id+"F0.wireOp",EDGE,"E13.13.10"),sQuery(id+"F0.wireOp",EDGE,"E13.13.11"),sQuery(id+"F0.wireOp",EDGE,"E13.14.0"),sQuery(id+"F0.wireOp",EDGE,"E13.14.1"),sQuery(id+"F0.wireOp",EDGE,"E13.14.2"),sQuery(id+"F0.wireOp",EDGE,"E13.14.3"),sQuery(id+"F0.wireOp",EDGE,"E13.14.4"),sQuery(id+"F0.wireOp",EDGE,"E13.14.5"),sQuery(id+"F0.wireOp",EDGE,"E13.14.6"),sQuery(id+"F0.wireOp",EDGE,"E13.14.7"),sQuery(id+"F0.wireOp",EDGE,"E13.14.8"),sQuery(id+"F0.wireOp",EDGE,"E13.14.9"),sQuery(id+"F0.wireOp",EDGE,"E13.14.10"),sQuery(id+"F0.wireOp",EDGE,"E13.14.11"),sQuery(id+"F0.wireOp",EDGE,"E13.15.0"),sQuery(id+"F0.wireOp",EDGE,"E13.15.1"),sQuery(id+"F0.wireOp",EDGE,"E13.15.2"),sQuery(id+"F0.wireOp",EDGE,"E13.15.3"),sQuery(id+"F0.wireOp",EDGE,"E13.15.4"),sQuery(id+"F0.wireOp",EDGE,"E13.15.5"),sQuery(id+"F0.wireOp",EDGE,"E13.15.6"),sQuery(id+"F0.wireOp",EDGE,"E13.15.7"),sQuery(id+"F0.wireOp",EDGE,"E13.15.8"),sQuery(id+"F0.wireOp",EDGE,"E13.15.9"),sQuery(id+"F0.wireOp",EDGE,"E13.15.10"),sQuery(id+"F0.wireOp",EDGE,"E13.15.11"),sQuery(id+"F0.wireOp",EDGE,"E13.16.0"),sQuery(id+"F0.wireOp",EDGE,"E13.16.1"),sQuery(id+"F0.wireOp",EDGE,"E13.16.2"),sQuery(id+"F0.wireOp",EDGE,"E13.16.3"),sQuery(id+"F0.wireOp",EDGE,"E13.16.4"),sQuery(id+"F0.wireOp",EDGE,"E13.16.5"),sQuery(id+"F0.wireOp",EDGE,"E13.16.6"),sQuery(id+"F0.wireOp",EDGE,"E13.16.7"),sQuery(id+"F0.wireOp",EDGE,"E13.16.8"),sQuery(id+"F0.wireOp",EDGE,"E13.16.9"),sQuery(id+"F0.wireOp",EDGE,"E13.16.10"),sQuery(id+"F0.wireOp",EDGE,"E13.16.11"),sQuery(id+"F0.wireOp",EDGE,"E13.17.0"),sQuery(id+"F0.wireOp",EDGE,"E13.17.1"),sQuery(id+"F0.wireOp",EDGE,"E13.17.2"),sQuery(id+"F0.wireOp",EDGE,"E13.17.3"),sQuery(id+"F0.wireOp",EDGE,"E13.17.4"),sQuery(id+"F0.wireOp",EDGE,"E13.17.5"),sQuery(id+"F0.wireOp",EDGE,"E13.17.6"),sQuery(id+"F0.wireOp",EDGE,"E13.17.7"),sQuery(id+"F0.wireOp",EDGE,"E13.17.8"),sQuery(id+"F0.wireOp",EDGE,"E13.17.9"),sQuery(id+"F0.wireOp",EDGE,"E13.17.10"),sQuery(id+"F0.wireOp",EDGE,"E13.17.11"),sQuery(id+"F0.wireOp",EDGE,"E13.18.0"),sQuery(id+"F0.wireOp",EDGE,"E13.18.1"),sQuery(id+"F0.wireOp",EDGE,"E13.18.2"),sQuery(id+"F0.wireOp",EDGE,"E13.18.3"),sQuery(id+"F0.wireOp",EDGE,"E13.18.4"),sQuery(id+"F0.wireOp",EDGE,"E13.18.5"),sQuery(id+"F0.wireOp",EDGE,"E13.18.6"),sQuery(id+"F0.wireOp",EDGE,"E13.18.7"),sQuery(id+"F0.wireOp",EDGE,"E13.18.8"),sQuery(id+"F0.wireOp",EDGE,"E13.18.9"),sQuery(id+"F0.wireOp",EDGE,"E13.18.10"),sQuery(id+"F0.wireOp",EDGE,"E13.18.11"),sQuery(id+"F0.wireOp",EDGE,"E13.19.0"),sQuery(id+"F0.wireOp",EDGE,"E13.19.1"),sQuery(id+"F0.wireOp",EDGE,"E13.19.2"),sQuery(id+"F0.wireOp",EDGE,"E13.19.3"),sQuery(id+"F0.wireOp",EDGE,"E13.19.4"),sQuery(id+"F0.wireOp",EDGE,"E13.19.5"),sQuery(id+"F0.wireOp",EDGE,"E13.19.6"),sQuery(id+"F0.wireOp",EDGE,"E13.19.7"),sQuery(id+"F0.wireOp",EDGE,"E13.19.8"),sQuery(id+"F0.wireOp",EDGE,"E13.19.9"),sQuery(id+"F0.wireOp",EDGE,"E13.19.10"),sQuery(id+"F0.wireOp",EDGE,"E13.19.11"),sQuery(id+"F0.wireOp",EDGE,"E13.20.0"),sQuery(id+"F0.wireOp",EDGE,"E13.20.1"),sQuery(id+"F0.wireOp",EDGE,"E13.20.2"),sQuery(id+"F0.wireOp",EDGE,"E13.20.3"),sQuery(id+"F0.wireOp",EDGE,"E13.20.4"),sQuery(id+"F0.wireOp",EDGE,"E13.20.5"),sQuery(id+"F0.wireOp",EDGE,"E13.20.6"),sQuery(id+"F0.wireOp",EDGE,"E13.20.7"),sQuery(id+"F0.wireOp",EDGE,"E13.20.8"),sQuery(id+"F0.wireOp",EDGE,"E13.20.9"),sQuery(id+"F0.wireOp",EDGE,"E13.20.10"),sQuery(id+"F0.wireOp",EDGE,"E13.20.11"),sQuery(id+"F0.wireOp",EDGE,"E13.21.0"),sQuery(id+"F0.wireOp",EDGE,"E13.21.1"),sQuery(id+"F0.wireOp",EDGE,"E13.21.2"),sQuery(id+"F0.wireOp",EDGE,"E13.21.3"),sQuery(id+"F0.wireOp",EDGE,"E13.21.4"),sQuery(id+"F0.wireOp",EDGE,"E13.21.5"),sQuery(id+"F0.wireOp",EDGE,"E13.21.6"),sQuery(id+"F0.wireOp",EDGE,"E13.21.7"),sQuery(id+"F0.wireOp",EDGE,"E13.21.8"),sQuery(id+"F0.wireOp",EDGE,"E13.21.9"),sQuery(id+"F0.wireOp",EDGE,"E13.21.10"),sQuery(id+"F0.wireOp",EDGE,"E13.21.11"),sQuery(id+"F0.wireOp",EDGE,"E13.22.0"),sQuery(id+"F0.wireOp",EDGE,"E13.22.1"),sQuery(id+"F0.wireOp",EDGE,"E13.22.2"),sQuery(id+"F0.wireOp",EDGE,"E13.22.3"),sQuery(id+"F0.wireOp",EDGE,"E13.22.4"),sQuery(id+"F0.wireOp",EDGE,"E13.22.5"),sQuery(id+"F0.wireOp",EDGE,"E13.22.6"),sQuery(id+"F0.wireOp",EDGE,"E13.22.7"),sQuery(id+"F0.wireOp",EDGE,"E13.22.8"),sQuery(id+"F0.wireOp",EDGE,"E13.22.9"),sQuery(id+"F0.wireOp",EDGE,"E13.22.10"),sQuery(id+"F0.wireOp",EDGE,"E13.22.11"),sQuery(id+"F0.wireOp",EDGE,"E13.23.0"),sQuery(id+"F0.wireOp",EDGE,"E13.23.1"),sQuery(id+"F0.wireOp",EDGE,"E13.23.2"),sQuery(id+"F0.wireOp",EDGE,"E13.23.3"),sQuery(id+"F0.wireOp",EDGE,"E13.23.4"),sQuery(id+"F0.wireOp",EDGE,"E13.23.5"),sQuery(id+"F0.wireOp",EDGE,"E13.23.6"),sQuery(id+"F0.wireOp",EDGE,"E13.23.7"),sQuery(id+"F0.wireOp",EDGE,"E13.23.8"),sQuery(id+"F0.wireOp",EDGE,"E13.23.9"),sQuery(id+"F0.wireOp",EDGE,"E13.23.10"),sQuery(id+"F0.wireOp",EDGE,"E13.23.11"),sQuery(id+"F0.wireOp",EDGE,"E13.24.0"),sQuery(id+"F0.wireOp",EDGE,"E13.24.1"),sQuery(id+"F0.wireOp",EDGE,"E13.24.2"),sQuery(id+"F0.wireOp",EDGE,"E13.24.3"),sQuery(id+"F0.wireOp",EDGE,"E13.24.4"),sQuery(id+"F0.wireOp",EDGE,"E13.24.5"),sQuery(id+"F0.wireOp",EDGE,"E13.24.6"),sQuery(id+"F0.wireOp",EDGE,"E13.24.7"),sQuery(id+"F0.wireOp",EDGE,"E13.24.8"),sQuery(id+"F0.wireOp",EDGE,"E13.24.9"),sQuery(id+"F0.wireOp",EDGE,"E13.24.10"),sQuery(id+"F0.wireOp",EDGE,"E13.24.11"),sQuery(id+"F0.wireOp",EDGE,"E13.25.0"),sQuery(id+"F0.wireOp",EDGE,"E13.25.1"),sQuery(id+"F0.wireOp",EDGE,"E13.25.2"),sQuery(id+"F0.wireOp",EDGE,"E13.25.3"),sQuery(id+"F0.wireOp",EDGE,"E13.25.4"),sQuery(id+"F0.wireOp",EDGE,"E13.25.5"),sQuery(id+"F0.wireOp",EDGE,"E13.25.6"),sQuery(id+"F0.wireOp",EDGE,"E13.25.7"),sQuery(id+"F0.wireOp",EDGE,"E13.25.8"),sQuery(id+"F0.wireOp",EDGE,"E13.25.9"),sQuery(id+"F0.wireOp",EDGE,"E13.25.10"),sQuery(id+"F0.wireOp",EDGE,"E13.25.11"),sQuery(id+"F0.wireOp",EDGE,"E13.26.0"),sQuery(id+"F0.wireOp",EDGE,"E13.26.1"),sQuery(id+"F0.wireOp",EDGE,"E13.26.2"),sQuery(id+"F0.wireOp",EDGE,"E13.26.3"),sQuery(id+"F0.wireOp",EDGE,"E13.26.4"),sQuery(id+"F0.wireOp",EDGE,"E13.26.5"),sQuery(id+"F0.wireOp",EDGE,"E13.26.6"),sQuery(id+"F0.wireOp",EDGE,"E13.26.7"),sQuery(id+"F0.wireOp",EDGE,"E13.26.8"),sQuery(id+"F0.wireOp",EDGE,"E13.26.9"),sQuery(id+"F0.wireOp",EDGE,"E13.26.10"),sQuery(id+"F0.wireOp",EDGE,"E13.26.11"),sQuery(id+"F0.wireOp",EDGE,"E13.27.0"),sQuery(id+"F0.wireOp",EDGE,"E13.27.1"),sQuery(id+"F0.wireOp",EDGE,"E13.27.2"),sQuery(id+"F0.wireOp",EDGE,"E13.27.3"),sQuery(id+"F0.wireOp",EDGE,"E13.27.4"),sQuery(id+"F0.wireOp",EDGE,"E13.27.5"),sQuery(id+"F0.wireOp",EDGE,"E13.27.6"),sQuery(id+"F0.wireOp",EDGE,"E13.27.7"),sQuery(id+"F0.wireOp",EDGE,"E13.27.8"),sQuery(id+"F0.wireOp",EDGE,"E13.27.9"),sQuery(id+"F0.wireOp",EDGE,"E13.27.10"),sQuery(id+"F0.wireOp",EDGE,"E13.27.11"),sQuery(id+"F0.wireOp",EDGE,"E13.28.0"),sQuery(id+"F0.wireOp",EDGE,"E13.28.1"),sQuery(id+"F0.wireOp",EDGE,"E13.28.2"),sQuery(id+"F0.wireOp",EDGE,"E13.28.3"),sQuery(id+"F0.wireOp",EDGE,"E13.28.4"),sQuery(id+"F0.wireOp",EDGE,"E13.28.5"),sQuery(id+"F0.wireOp",EDGE,"E13.28.6"),sQuery(id+"F0.wireOp",EDGE,"E13.28.7"),sQuery(id+"F0.wireOp",EDGE,"E13.28.8"),sQuery(id+"F0.wireOp",EDGE,"E13.28.9"),sQuery(id+"F0.wireOp",EDGE,"E13.28.10"),sQuery(id+"F0.wireOp",EDGE,"E13.28.11"),sQuery(id+"F0.wireOp",EDGE,"E13.29.0"),sQuery(id+"F0.wireOp",EDGE,"E13.29.1"),sQuery(id+"F0.wireOp",EDGE,"E13.29.2"),sQuery(id+"F0.wireOp",EDGE,"E13.29.3"),sQuery(id+"F0.wireOp",EDGE,"E13.29.4"),sQuery(id+"F0.wireOp",EDGE,"E13.29.5"),sQuery(id+"F0.wireOp",EDGE,"E13.29.6"),sQuery(id+"F0.wireOp",EDGE,"E13.29.7"),sQuery(id+"F0.wireOp",EDGE,"E13.29.8"),sQuery(id+"F0.wireOp",EDGE,"E13.29.9"),sQuery(id+"F0.wireOp",EDGE,"E13.29.10"),sQuery(id+"F0.wireOp",EDGE,"E13.29.11"),sQuery(id+"F0.wireOp",EDGE,"E13.30.0"),sQuery(id+"F0.wireOp",EDGE,"E13.30.1"),sQuery(id+"F0.wireOp",EDGE,"E13.30.2"),sQuery(id+"F0.wireOp",EDGE,"E13.30.3"),sQuery(id+"F0.wireOp",EDGE,"E13.30.4"),sQuery(id+"F0.wireOp",EDGE,"E13.30.5"),sQuery(id+"F0.wireOp",EDGE,"E13.30.6"),sQuery(id+"F0.wireOp",EDGE,"E13.30.7"),sQuery(id+"F0.wireOp",EDGE,"E13.30.8"),sQuery(id+"F0.wireOp",EDGE,"E13.30.9"),sQuery(id+"F0.wireOp",EDGE,"E13.30.10"),sQuery(id+"F0.wireOp",EDGE,"E13.30.11"),sQuery(id+"F0.wireOp",EDGE,"E13.31.0"),sQuery(id+"F0.wireOp",EDGE,"E13.31.1"),sQuery(id+"F0.wireOp",EDGE,"E13.31.2"),sQuery(id+"F0.wireOp",EDGE,"E13.31.3"),sQuery(id+"F0.wireOp",EDGE,"E13.31.4"),sQuery(id+"F0.wireOp",EDGE,"E13.31.5"),sQuery(id+"F0.wireOp",EDGE,"E13.31.6"),sQuery(id+"F0.wireOp",EDGE,"E13.31.7"),sQuery(id+"F0.wireOp",EDGE,"E13.31.8"),sQuery(id+"F0.wireOp",EDGE,"E13.31.9"),sQuery(id+"F0.wireOp",EDGE,"E13.31.10"),sQuery(id+"F0.wireOp",EDGE,"E13.31.11"),sQuery(id+"F0.wireOp",EDGE,"E13.32.0"),sQuery(id+"F0.wireOp",EDGE,"E13.32.1"),sQuery(id+"F0.wireOp",EDGE,"E13.32.2"),sQuery(id+"F0.wireOp",EDGE,"E13.32.3"),sQuery(id+"F0.wireOp",EDGE,"E13.32.4"),sQuery(id+"F0.wireOp",EDGE,"E13.32.5"),sQuery(id+"F0.wireOp",EDGE,"E13.32.6"),sQuery(id+"F0.wireOp",EDGE,"E13.32.7"),sQuery(id+"F0.wireOp",EDGE,"E13.32.8"),sQuery(id+"F0.wireOp",EDGE,"E13.32.9"),sQuery(id+"F0.wireOp",EDGE,"E13.32.10"),sQuery(id+"F0.wireOp",EDGE,"E13.32.11"),sQuery(id+"F0.wireOp",EDGE,"E13.33.0"),sQuery(id+"F0.wireOp",EDGE,"E13.33.1"),sQuery(id+"F0.wireOp",EDGE,"E13.33.2"),sQuery(id+"F0.wireOp",EDGE,"E13.33.3"),sQuery(id+"F0.wireOp",EDGE,"E13.33.4"),sQuery(id+"F0.wireOp",EDGE,"E13.33.5"),sQuery(id+"F0.wireOp",EDGE,"E13.33.6"),sQuery(id+"F0.wireOp",EDGE,"E13.33.7"),sQuery(id+"F0.wireOp",EDGE,"E13.33.8"),sQuery(id+"F0.wireOp",EDGE,"E13.33.9"),sQuery(id+"F0.wireOp",EDGE,"E13.33.10"),sQuery(id+"F0.wireOp",EDGE,"E13.33.11"),sQuery(id+"F0.wireOp",EDGE,"E13.34.0"),sQuery(id+"F0.wireOp",EDGE,"E13.34.1"),sQuery(id+"F0.wireOp",EDGE,"E13.34.2"),sQuery(id+"F0.wireOp",EDGE,"E13.34.3"),sQuery(id+"F0.wireOp",EDGE,"E13.34.4"),sQuery(id+"F0.wireOp",EDGE,"E13.34.5"),sQuery(id+"F0.wireOp",EDGE,"E13.34.6"),sQuery(id+"F0.wireOp",EDGE,"E13.34.7"),sQuery(id+"F0.wireOp",EDGE,"E13.34.8"),sQuery(id+"F0.wireOp",EDGE,"E13.34.9"),sQuery(id+"F0.wireOp",EDGE,"E13.34.10"),sQuery(id+"F0.wireOp",EDGE,"E13.34.11"),sQuery(id+"F0.wireOp",EDGE,"E13.35.0"),sQuery(id+"F0.wireOp",EDGE,"E13.35.1"),sQuery(id+"F0.wireOp",EDGE,"E13.35.2"),sQuery(id+"F0.wireOp",EDGE,"E13.35.3"),sQuery(id+"F0.wireOp",EDGE,"E13.35.4"),sQuery(id+"F0.wireOp",EDGE,"E13.35.5"),sQuery(id+"F0.wireOp",EDGE,"E13.35.6"),sQuery(id+"F0.wireOp",EDGE,"E13.35.7"),sQuery(id+"F0.wireOp",EDGE,"E13.35.8"),sQuery(id+"F0.wireOp",EDGE,"E13.35.9"),sQuery(id+"F0.wireOp",EDGE,"E13.35.10"),sQuery(id+"F0.wireOp",EDGE,"E13.35.11"),sQuery(id+"F0.wireOp",EDGE,"E14.trimOffspring"),sQuery(id+"F0.wireOp",EDGE,"E15.trimOffspring"),sQuery(id+"F0.wireOp",EDGE,"E16.trimOffspring"),sQuery(id+"F0.wireOp",EDGE,"E17.trimOffspring"),sQuery(id+"F0.wireOp",EDGE,"E18.trimOffspring"),sQuery(id+"F0.wireOp",EDGE,"E19.trimOffspring"),sQuery(id+"F0.wireOp",EDGE,"E20.trimOffspring"),sQuery(id+"F0.wireOp",EDGE,"E21.trimOffspring"),sQuery(id+"F0.wireOp",EDGE,"E22.trimOffspring"),sQuery(id+"F0.wireOp",EDGE,"E23.trimOffspring"),sQuery(id+"F0.wireOp",EDGE,"E24.trimOffspring"),sQuery(id+"F0.wireOp",EDGE,"E25.trimOffspring"),sQuery(id+"F0.wireOp",EDGE,"E26.trimOffspring"),sQuery(id+"F0.wireOp",EDGE,"E27.trimOffspring"),sQuery(id+"F0.wireOp",EDGE,"E28.trimOffspring"),sQuery(id+"F0.wireOp",EDGE,"E29.trimOffspring"),sQuery(id+"F0.wireOp",EDGE,"E30.trimOffspring"),sQuery(id+"F0.wireOp",EDGE,"E31.trimOffspring"),sQuery(id+"F0.wireOp",EDGE,"E32.trimOffspring"),sQuery(id+"F0.wireOp",EDGE,"E33.trimOffspring"),sQuery(id+"F0.wireOp",EDGE,"E34.trimOffspring"),sQuery(id+"F0.wireOp",EDGE,"E35.trimOffspring"),sQuery(id+"F0.wireOp",EDGE,"E36.trimOffspring"),sQuery(id+"F0.wireOp",EDGE,"E37.trimOffspring"),sQuery(id+"F0.wireOp",EDGE,"E38.trimOffspring"),sQuery(id+"F0.wireOp",EDGE,"E39.trimOffspring"),sQuery(id+"F0.wireOp",EDGE,"E40.trimOffspring"),sQuery(id+"F0.wireOp",EDGE,"E41.trimOffspring"),sQuery(id+"F0.wireOp",EDGE,"E42.trimOffspring"),sQuery(id+"F0.wireOp",EDGE,"E43.trimOffspring"),sQuery(id+"F0.wireOp",EDGE,"E44.trimOffspring"),sQuery(id+"F0.wireOp",EDGE,"E45.trimOffspring"),sQuery(id+"F0.wireOp",EDGE,"E46.trimOffspring"),sQuery(id+"F0.wireOp",EDGE,"E47.trimOffspring"),sQuery(id+"F0.wireOp",EDGE,"E48.trimOffspring"),sQuery(id+"F0.wireOp",EDGE,"E49")])],"isStart":false});
            shell(context, id + "F2", {"entities" : qUnion([Q0]), "thickness" : 6.35 * mm});
        }
        {
            var Q0;
            Q0=makeQuery(id+"F2.opShell","OFFSET_FACE",FACE,{"disambiguationData":[OSD([sQuery(id+"F0.wireOp",EDGE,"E1.trimOffspring"),sQuery(id+"F0.wireOp",EDGE,"E2"),sQuery(id+"F0.wireOp",EDGE,"E3"),sQuery(id+"F0.wireOp",EDGE,"E4.MirrorCS"),sQuery(id+"F0.wireOp",EDGE,"E5.MirrorCS"),sQuery(id+"F0.wireOp",EDGE,"E6.MirrorCS"),sQuery(id+"F0.wireOp",EDGE,"E7.filletArc"),sQuery(id+"F0.wireOp",EDGE,"E8.filletArc"),sQuery(id+"F0.wireOp",EDGE,"E9.filletArc"),sQuery(id+"F0.wireOp",EDGE,"E10.filletArc"),sQuery(id+"F0.wireOp",EDGE,"E11.filletArc"),sQuery(id+"F0.wireOp",EDGE,"E12.filletArc"),sQuery(id+"F0.wireOp",EDGE,"E13.1.0"),sQuery(id+"F0.wireOp",EDGE,"E13.1.1"),sQuery(id+"F0.wireOp",EDGE,"E13.1.2"),sQuery(id+"F0.wireOp",EDGE,"E13.1.3"),sQuery(id+"F0.wireOp",EDGE,"E13.1.4"),sQuery(id+"F0.wireOp",EDGE,"E13.1.5"),sQuery(id+"F0.wireOp",EDGE,"E13.1.6"),sQuery(id+"F0.wireOp",EDGE,"E13.1.7"),sQuery(id+"F0.wireOp",EDGE,"E13.1.8"),sQuery(id+"F0.wireOp",EDGE,"E13.1.9"),sQuery(id+"F0.wireOp",EDGE,"E13.1.10"),sQuery(id+"F0.wireOp",EDGE,"E13.1.11"),sQuery(id+"F0.wireOp",EDGE,"E13.2.0"),sQuery(id+"F0.wireOp",EDGE,"E13.2.1"),sQuery(id+"F0.wireOp",EDGE,"E13.2.2"),sQuery(id+"F0.wireOp",EDGE,"E13.2.3"),sQuery(id+"F0.wireOp",EDGE,"E13.2.4"),sQuery(id+"F0.wireOp",EDGE,"E13.2.5"),sQuery(id+"F0.wireOp",EDGE,"E13.2.6"),sQuery(id+"F0.wireOp",EDGE,"E13.2.7"),sQuery(id+"F0.wireOp",EDGE,"E13.2.8"),sQuery(id+"F0.wireOp",EDGE,"E13.2.9"),sQuery(id+"F0.wireOp",EDGE,"E13.2.10"),sQuery(id+"F0.wireOp",EDGE,"E13.2.11"),sQuery(id+"F0.wireOp",EDGE,"E13.3.0"),sQuery(id+"F0.wireOp",EDGE,"E13.3.1"),sQuery(id+"F0.wireOp",EDGE,"E13.3.2"),sQuery(id+"F0.wireOp",EDGE,"E13.3.3"),sQuery(id+"F0.wireOp",EDGE,"E13.3.4"),sQuery(id+"F0.wireOp",EDGE,"E13.3.5"),sQuery(id+"F0.wireOp",EDGE,"E13.3.6"),sQuery(id+"F0.wireOp",EDGE,"E13.3.7"),sQuery(id+"F0.wireOp",EDGE,"E13.3.8"),sQuery(id+"F0.wireOp",EDGE,"E13.3.9"),sQuery(id+"F0.wireOp",EDGE,"E13.3.10"),sQuery(id+"F0.wireOp",EDGE,"E13.3.11"),sQuery(id+"F0.wireOp",EDGE,"E13.4.0"),sQuery(id+"F0.wireOp",EDGE,"E13.4.1"),sQuery(id+"F0.wireOp",EDGE,"E13.4.2"),sQuery(id+"F0.wireOp",EDGE,"E13.4.3"),sQuery(id+"F0.wireOp",EDGE,"E13.4.4"),sQuery(id+"F0.wireOp",EDGE,"E13.4.5"),sQuery(id+"F0.wireOp",EDGE,"E13.4.6"),sQuery(id+"F0.wireOp",EDGE,"E13.4.7"),sQuery(id+"F0.wireOp",EDGE,"E13.4.8"),sQuery(id+"F0.wireOp",EDGE,"E13.4.9"),sQuery(id+"F0.wireOp",EDGE,"E13.4.10"),sQuery(id+"F0.wireOp",EDGE,"E13.4.11"),sQuery(id+"F0.wireOp",EDGE,"E13.5.0"),sQuery(id+"F0.wireOp",EDGE,"E13.5.1"),sQuery(id+"F0.wireOp",EDGE,"E13.5.2"),sQuery(id+"F0.wireOp",EDGE,"E13.5.3"),sQuery(id+"F0.wireOp",EDGE,"E13.5.4"),sQuery(id+"F0.wireOp",EDGE,"E13.5.5"),sQuery(id+"F0.wireOp",EDGE,"E13.5.6"),sQuery(id+"F0.wireOp",EDGE,"E13.5.7"),sQuery(id+"F0.wireOp",EDGE,"E13.5.8"),sQuery(id+"F0.wireOp",EDGE,"E13.5.9"),sQuery(id+"F0.wireOp",EDGE,"E13.5.10"),sQuery(id+"F0.wireOp",EDGE,"E13.5.11"),sQuery(id+"F0.wireOp",EDGE,"E13.6.0"),sQuery(id+"F0.wireOp",EDGE,"E13.6.1"),sQuery(id+"F0.wireOp",EDGE,"E13.6.2"),sQuery(id+"F0.wireOp",EDGE,"E13.6.3"),sQuery(id+"F0.wireOp",EDGE,"E13.6.4"),sQuery(id+"F0.wireOp",EDGE,"E13.6.5"),sQuery(id+"F0.wireOp",EDGE,"E13.6.6"),sQuery(id+"F0.wireOp",EDGE,"E13.6.7"),sQuery(id+"F0.wireOp",EDGE,"E13.6.8"),sQuery(id+"F0.wireOp",EDGE,"E13.6.9"),sQuery(id+"F0.wireOp",EDGE,"E13.6.10"),sQuery(id+"F0.wireOp",EDGE,"E13.6.11"),sQuery(id+"F0.wireOp",EDGE,"E13.7.0"),sQuery(id+"F0.wireOp",EDGE,"E13.7.1"),sQuery(id+"F0.wireOp",EDGE,"E13.7.2"),sQuery(id+"F0.wireOp",EDGE,"E13.7.3"),sQuery(id+"F0.wireOp",EDGE,"E13.7.4"),sQuery(id+"F0.wireOp",EDGE,"E13.7.5"),sQuery(id+"F0.wireOp",EDGE,"E13.7.6"),sQuery(id+"F0.wireOp",EDGE,"E13.7.7"),sQuery(id+"F0.wireOp",EDGE,"E13.7.8"),sQuery(id+"F0.wireOp",EDGE,"E13.7.9"),sQuery(id+"F0.wireOp",EDGE,"E13.7.10"),sQuery(id+"F0.wireOp",EDGE,"E13.7.11"),sQuery(id+"F0.wireOp",EDGE,"E13.8.0"),sQuery(id+"F0.wireOp",EDGE,"E13.8.1"),sQuery(id+"F0.wireOp",EDGE,"E13.8.2"),sQuery(id+"F0.wireOp",EDGE,"E13.8.3"),sQuery(id+"F0.wireOp",EDGE,"E13.8.4"),sQuery(id+"F0.wireOp",EDGE,"E13.8.5"),sQuery(id+"F0.wireOp",EDGE,"E13.8.6"),sQuery(id+"F0.wireOp",EDGE,"E13.8.7"),sQuery(id+"F0.wireOp",EDGE,"E13.8.8"),sQuery(id+"F0.wireOp",EDGE,"E13.8.9"),sQuery(id+"F0.wireOp",EDGE,"E13.8.10"),sQuery(id+"F0.wireOp",EDGE,"E13.8.11"),sQuery(id+"F0.wireOp",EDGE,"E13.9.0"),sQuery(id+"F0.wireOp",EDGE,"E13.9.1"),sQuery(id+"F0.wireOp",EDGE,"E13.9.2"),sQuery(id+"F0.wireOp",EDGE,"E13.9.3"),sQuery(id+"F0.wireOp",EDGE,"E13.9.4"),sQuery(id+"F0.wireOp",EDGE,"E13.9.5"),sQuery(id+"F0.wireOp",EDGE,"E13.9.6"),sQuery(id+"F0.wireOp",EDGE,"E13.9.7"),sQuery(id+"F0.wireOp",EDGE,"E13.9.8"),sQuery(id+"F0.wireOp",EDGE,"E13.9.9"),sQuery(id+"F0.wireOp",EDGE,"E13.9.10"),sQuery(id+"F0.wireOp",EDGE,"E13.9.11"),sQuery(id+"F0.wireOp",EDGE,"E13.10.0"),sQuery(id+"F0.wireOp",EDGE,"E13.10.1"),sQuery(id+"F0.wireOp",EDGE,"E13.10.2"),sQuery(id+"F0.wireOp",EDGE,"E13.10.3"),sQuery(id+"F0.wireOp",EDGE,"E13.10.4"),sQuery(id+"F0.wireOp",EDGE,"E13.10.5"),sQuery(id+"F0.wireOp",EDGE,"E13.10.6"),sQuery(id+"F0.wireOp",EDGE,"E13.10.7"),sQuery(id+"F0.wireOp",EDGE,"E13.10.8"),sQuery(id+"F0.wireOp",EDGE,"E13.10.9"),sQuery(id+"F0.wireOp",EDGE,"E13.10.10"),sQuery(id+"F0.wireOp",EDGE,"E13.10.11"),sQuery(id+"F0.wireOp",EDGE,"E13.11.0"),sQuery(id+"F0.wireOp",EDGE,"E13.11.1"),sQuery(id+"F0.wireOp",EDGE,"E13.11.2"),sQuery(id+"F0.wireOp",EDGE,"E13.11.3"),sQuery(id+"F0.wireOp",EDGE,"E13.11.4"),sQuery(id+"F0.wireOp",EDGE,"E13.11.5"),sQuery(id+"F0.wireOp",EDGE,"E13.11.6"),sQuery(id+"F0.wireOp",EDGE,"E13.11.7"),sQuery(id+"F0.wireOp",EDGE,"E13.11.8"),sQuery(id+"F0.wireOp",EDGE,"E13.11.9"),sQuery(id+"F0.wireOp",EDGE,"E13.11.10"),sQuery(id+"F0.wireOp",EDGE,"E13.11.11"),sQuery(id+"F0.wireOp",EDGE,"E13.12.0"),sQuery(id+"F0.wireOp",EDGE,"E13.12.1"),sQuery(id+"F0.wireOp",EDGE,"E13.12.2"),sQuery(id+"F0.wireOp",EDGE,"E13.12.3"),sQuery(id+"F0.wireOp",EDGE,"E13.12.4"),sQuery(id+"F0.wireOp",EDGE,"E13.12.5"),sQuery(id+"F0.wireOp",EDGE,"E13.12.6"),sQuery(id+"F0.wireOp",EDGE,"E13.12.7"),sQuery(id+"F0.wireOp",EDGE,"E13.12.8"),sQuery(id+"F0.wireOp",EDGE,"E13.12.9"),sQuery(id+"F0.wireOp",EDGE,"E13.12.10"),sQuery(id+"F0.wireOp",EDGE,"E13.12.11"),sQuery(id+"F0.wireOp",EDGE,"E13.13.0"),sQuery(id+"F0.wireOp",EDGE,"E13.13.1"),sQuery(id+"F0.wireOp",EDGE,"E13.13.2"),sQuery(id+"F0.wireOp",EDGE,"E13.13.3"),sQuery(id+"F0.wireOp",EDGE,"E13.13.4"),sQuery(id+"F0.wireOp",EDGE,"E13.13.5"),sQuery(id+"F0.wireOp",EDGE,"E13.13.6"),sQuery(id+"F0.wireOp",EDGE,"E13.13.7"),sQuery(id+"F0.wireOp",EDGE,"E13.13.8"),sQuery(id+"F0.wireOp",EDGE,"E13.13.9"),sQuery(id+"F0.wireOp",EDGE,"E13.13.10"),sQuery(id+"F0.wireOp",EDGE,"E13.13.11"),sQuery(id+"F0.wireOp",EDGE,"E13.14.0"),sQuery(id+"F0.wireOp",EDGE,"E13.14.1"),sQuery(id+"F0.wireOp",EDGE,"E13.14.2"),sQuery(id+"F0.wireOp",EDGE,"E13.14.3"),sQuery(id+"F0.wireOp",EDGE,"E13.14.4"),sQuery(id+"F0.wireOp",EDGE,"E13.14.5"),sQuery(id+"F0.wireOp",EDGE,"E13.14.6"),sQuery(id+"F0.wireOp",EDGE,"E13.14.7"),sQuery(id+"F0.wireOp",EDGE,"E13.14.8"),sQuery(id+"F0.wireOp",EDGE,"E13.14.9"),sQuery(id+"F0.wireOp",EDGE,"E13.14.10"),sQuery(id+"F0.wireOp",EDGE,"E13.14.11"),sQuery(id+"F0.wireOp",EDGE,"E13.15.0"),sQuery(id+"F0.wireOp",EDGE,"E13.15.1"),sQuery(id+"F0.wireOp",EDGE,"E13.15.2"),sQuery(id+"F0.wireOp",EDGE,"E13.15.3"),sQuery(id+"F0.wireOp",EDGE,"E13.15.4"),sQuery(id+"F0.wireOp",EDGE,"E13.15.5"),sQuery(id+"F0.wireOp",EDGE,"E13.15.6"),sQuery(id+"F0.wireOp",EDGE,"E13.15.7"),sQuery(id+"F0.wireOp",EDGE,"E13.15.8"),sQuery(id+"F0.wireOp",EDGE,"E13.15.9"),sQuery(id+"F0.wireOp",EDGE,"E13.15.10"),sQuery(id+"F0.wireOp",EDGE,"E13.15.11"),sQuery(id+"F0.wireOp",EDGE,"E13.16.0"),sQuery(id+"F0.wireOp",EDGE,"E13.16.1"),sQuery(id+"F0.wireOp",EDGE,"E13.16.2"),sQuery(id+"F0.wireOp",EDGE,"E13.16.3"),sQuery(id+"F0.wireOp",EDGE,"E13.16.4"),sQuery(id+"F0.wireOp",EDGE,"E13.16.5"),sQuery(id+"F0.wireOp",EDGE,"E13.16.6"),sQuery(id+"F0.wireOp",EDGE,"E13.16.7"),sQuery(id+"F0.wireOp",EDGE,"E13.16.8"),sQuery(id+"F0.wireOp",EDGE,"E13.16.9"),sQuery(id+"F0.wireOp",EDGE,"E13.16.10"),sQuery(id+"F0.wireOp",EDGE,"E13.16.11"),sQuery(id+"F0.wireOp",EDGE,"E13.17.0"),sQuery(id+"F0.wireOp",EDGE,"E13.17.1"),sQuery(id+"F0.wireOp",EDGE,"E13.17.2"),sQuery(id+"F0.wireOp",EDGE,"E13.17.3"),sQuery(id+"F0.wireOp",EDGE,"E13.17.4"),sQuery(id+"F0.wireOp",EDGE,"E13.17.5"),sQuery(id+"F0.wireOp",EDGE,"E13.17.6"),sQuery(id+"F0.wireOp",EDGE,"E13.17.7"),sQuery(id+"F0.wireOp",EDGE,"E13.17.8"),sQuery(id+"F0.wireOp",EDGE,"E13.17.9"),sQuery(id+"F0.wireOp",EDGE,"E13.17.10"),sQuery(id+"F0.wireOp",EDGE,"E13.17.11"),sQuery(id+"F0.wireOp",EDGE,"E13.18.0"),sQuery(id+"F0.wireOp",EDGE,"E13.18.1"),sQuery(id+"F0.wireOp",EDGE,"E13.18.2"),sQuery(id+"F0.wireOp",EDGE,"E13.18.3"),sQuery(id+"F0.wireOp",EDGE,"E13.18.4"),sQuery(id+"F0.wireOp",EDGE,"E13.18.5"),sQuery(id+"F0.wireOp",EDGE,"E13.18.6"),sQuery(id+"F0.wireOp",EDGE,"E13.18.7"),sQuery(id+"F0.wireOp",EDGE,"E13.18.8"),sQuery(id+"F0.wireOp",EDGE,"E13.18.9"),sQuery(id+"F0.wireOp",EDGE,"E13.18.10"),sQuery(id+"F0.wireOp",EDGE,"E13.18.11"),sQuery(id+"F0.wireOp",EDGE,"E13.19.0"),sQuery(id+"F0.wireOp",EDGE,"E13.19.1"),sQuery(id+"F0.wireOp",EDGE,"E13.19.2"),sQuery(id+"F0.wireOp",EDGE,"E13.19.3"),sQuery(id+"F0.wireOp",EDGE,"E13.19.4"),sQuery(id+"F0.wireOp",EDGE,"E13.19.5"),sQuery(id+"F0.wireOp",EDGE,"E13.19.6"),sQuery(id+"F0.wireOp",EDGE,"E13.19.7"),sQuery(id+"F0.wireOp",EDGE,"E13.19.8"),sQuery(id+"F0.wireOp",EDGE,"E13.19.9"),sQuery(id+"F0.wireOp",EDGE,"E13.19.10"),sQuery(id+"F0.wireOp",EDGE,"E13.19.11"),sQuery(id+"F0.wireOp",EDGE,"E13.20.0"),sQuery(id+"F0.wireOp",EDGE,"E13.20.1"),sQuery(id+"F0.wireOp",EDGE,"E13.20.2"),sQuery(id+"F0.wireOp",EDGE,"E13.20.3"),sQuery(id+"F0.wireOp",EDGE,"E13.20.4"),sQuery(id+"F0.wireOp",EDGE,"E13.20.5"),sQuery(id+"F0.wireOp",EDGE,"E13.20.6"),sQuery(id+"F0.wireOp",EDGE,"E13.20.7"),sQuery(id+"F0.wireOp",EDGE,"E13.20.8"),sQuery(id+"F0.wireOp",EDGE,"E13.20.9"),sQuery(id+"F0.wireOp",EDGE,"E13.20.10"),sQuery(id+"F0.wireOp",EDGE,"E13.20.11"),sQuery(id+"F0.wireOp",EDGE,"E13.21.0"),sQuery(id+"F0.wireOp",EDGE,"E13.21.1"),sQuery(id+"F0.wireOp",EDGE,"E13.21.2"),sQuery(id+"F0.wireOp",EDGE,"E13.21.3"),sQuery(id+"F0.wireOp",EDGE,"E13.21.4"),sQuery(id+"F0.wireOp",EDGE,"E13.21.5"),sQuery(id+"F0.wireOp",EDGE,"E13.21.6"),sQuery(id+"F0.wireOp",EDGE,"E13.21.7"),sQuery(id+"F0.wireOp",EDGE,"E13.21.8"),sQuery(id+"F0.wireOp",EDGE,"E13.21.9"),sQuery(id+"F0.wireOp",EDGE,"E13.21.10"),sQuery(id+"F0.wireOp",EDGE,"E13.21.11"),sQuery(id+"F0.wireOp",EDGE,"E13.22.0"),sQuery(id+"F0.wireOp",EDGE,"E13.22.1"),sQuery(id+"F0.wireOp",EDGE,"E13.22.2"),sQuery(id+"F0.wireOp",EDGE,"E13.22.3"),sQuery(id+"F0.wireOp",EDGE,"E13.22.4"),sQuery(id+"F0.wireOp",EDGE,"E13.22.5"),sQuery(id+"F0.wireOp",EDGE,"E13.22.6"),sQuery(id+"F0.wireOp",EDGE,"E13.22.7"),sQuery(id+"F0.wireOp",EDGE,"E13.22.8"),sQuery(id+"F0.wireOp",EDGE,"E13.22.9"),sQuery(id+"F0.wireOp",EDGE,"E13.22.10"),sQuery(id+"F0.wireOp",EDGE,"E13.22.11"),sQuery(id+"F0.wireOp",EDGE,"E13.23.0"),sQuery(id+"F0.wireOp",EDGE,"E13.23.1"),sQuery(id+"F0.wireOp",EDGE,"E13.23.2"),sQuery(id+"F0.wireOp",EDGE,"E13.23.3"),sQuery(id+"F0.wireOp",EDGE,"E13.23.4"),sQuery(id+"F0.wireOp",EDGE,"E13.23.5"),sQuery(id+"F0.wireOp",EDGE,"E13.23.6"),sQuery(id+"F0.wireOp",EDGE,"E13.23.7"),sQuery(id+"F0.wireOp",EDGE,"E13.23.8"),sQuery(id+"F0.wireOp",EDGE,"E13.23.9"),sQuery(id+"F0.wireOp",EDGE,"E13.23.10"),sQuery(id+"F0.wireOp",EDGE,"E13.23.11"),sQuery(id+"F0.wireOp",EDGE,"E13.24.0"),sQuery(id+"F0.wireOp",EDGE,"E13.24.1"),sQuery(id+"F0.wireOp",EDGE,"E13.24.2"),sQuery(id+"F0.wireOp",EDGE,"E13.24.3"),sQuery(id+"F0.wireOp",EDGE,"E13.24.4"),sQuery(id+"F0.wireOp",EDGE,"E13.24.5"),sQuery(id+"F0.wireOp",EDGE,"E13.24.6"),sQuery(id+"F0.wireOp",EDGE,"E13.24.7"),sQuery(id+"F0.wireOp",EDGE,"E13.24.8"),sQuery(id+"F0.wireOp",EDGE,"E13.24.9"),sQuery(id+"F0.wireOp",EDGE,"E13.24.10"),sQuery(id+"F0.wireOp",EDGE,"E13.24.11"),sQuery(id+"F0.wireOp",EDGE,"E13.25.0"),sQuery(id+"F0.wireOp",EDGE,"E13.25.1"),sQuery(id+"F0.wireOp",EDGE,"E13.25.2"),sQuery(id+"F0.wireOp",EDGE,"E13.25.3"),sQuery(id+"F0.wireOp",EDGE,"E13.25.4"),sQuery(id+"F0.wireOp",EDGE,"E13.25.5"),sQuery(id+"F0.wireOp",EDGE,"E13.25.6"),sQuery(id+"F0.wireOp",EDGE,"E13.25.7"),sQuery(id+"F0.wireOp",EDGE,"E13.25.8"),sQuery(id+"F0.wireOp",EDGE,"E13.25.9"),sQuery(id+"F0.wireOp",EDGE,"E13.25.10"),sQuery(id+"F0.wireOp",EDGE,"E13.25.11"),sQuery(id+"F0.wireOp",EDGE,"E13.26.0"),sQuery(id+"F0.wireOp",EDGE,"E13.26.1"),sQuery(id+"F0.wireOp",EDGE,"E13.26.2"),sQuery(id+"F0.wireOp",EDGE,"E13.26.3"),sQuery(id+"F0.wireOp",EDGE,"E13.26.4"),sQuery(id+"F0.wireOp",EDGE,"E13.26.5"),sQuery(id+"F0.wireOp",EDGE,"E13.26.6"),sQuery(id+"F0.wireOp",EDGE,"E13.26.7"),sQuery(id+"F0.wireOp",EDGE,"E13.26.8"),sQuery(id+"F0.wireOp",EDGE,"E13.26.9"),sQuery(id+"F0.wireOp",EDGE,"E13.26.10"),sQuery(id+"F0.wireOp",EDGE,"E13.26.11"),sQuery(id+"F0.wireOp",EDGE,"E13.27.0"),sQuery(id+"F0.wireOp",EDGE,"E13.27.1"),sQuery(id+"F0.wireOp",EDGE,"E13.27.2"),sQuery(id+"F0.wireOp",EDGE,"E13.27.3"),sQuery(id+"F0.wireOp",EDGE,"E13.27.4"),sQuery(id+"F0.wireOp",EDGE,"E13.27.5"),sQuery(id+"F0.wireOp",EDGE,"E13.27.6"),sQuery(id+"F0.wireOp",EDGE,"E13.27.7"),sQuery(id+"F0.wireOp",EDGE,"E13.27.8"),sQuery(id+"F0.wireOp",EDGE,"E13.27.9"),sQuery(id+"F0.wireOp",EDGE,"E13.27.10"),sQuery(id+"F0.wireOp",EDGE,"E13.27.11"),sQuery(id+"F0.wireOp",EDGE,"E13.28.0"),sQuery(id+"F0.wireOp",EDGE,"E13.28.1"),sQuery(id+"F0.wireOp",EDGE,"E13.28.2"),sQuery(id+"F0.wireOp",EDGE,"E13.28.3"),sQuery(id+"F0.wireOp",EDGE,"E13.28.4"),sQuery(id+"F0.wireOp",EDGE,"E13.28.5"),sQuery(id+"F0.wireOp",EDGE,"E13.28.6"),sQuery(id+"F0.wireOp",EDGE,"E13.28.7"),sQuery(id+"F0.wireOp",EDGE,"E13.28.8"),sQuery(id+"F0.wireOp",EDGE,"E13.28.9"),sQuery(id+"F0.wireOp",EDGE,"E13.28.10"),sQuery(id+"F0.wireOp",EDGE,"E13.28.11"),sQuery(id+"F0.wireOp",EDGE,"E13.29.0"),sQuery(id+"F0.wireOp",EDGE,"E13.29.1"),sQuery(id+"F0.wireOp",EDGE,"E13.29.2"),sQuery(id+"F0.wireOp",EDGE,"E13.29.3"),sQuery(id+"F0.wireOp",EDGE,"E13.29.4"),sQuery(id+"F0.wireOp",EDGE,"E13.29.5"),sQuery(id+"F0.wireOp",EDGE,"E13.29.6"),sQuery(id+"F0.wireOp",EDGE,"E13.29.7"),sQuery(id+"F0.wireOp",EDGE,"E13.29.8"),sQuery(id+"F0.wireOp",EDGE,"E13.29.9"),sQuery(id+"F0.wireOp",EDGE,"E13.29.10"),sQuery(id+"F0.wireOp",EDGE,"E13.29.11"),sQuery(id+"F0.wireOp",EDGE,"E13.30.0"),sQuery(id+"F0.wireOp",EDGE,"E13.30.1"),sQuery(id+"F0.wireOp",EDGE,"E13.30.2"),sQuery(id+"F0.wireOp",EDGE,"E13.30.3"),sQuery(id+"F0.wireOp",EDGE,"E13.30.4"),sQuery(id+"F0.wireOp",EDGE,"E13.30.5"),sQuery(id+"F0.wireOp",EDGE,"E13.30.6"),sQuery(id+"F0.wireOp",EDGE,"E13.30.7"),sQuery(id+"F0.wireOp",EDGE,"E13.30.8"),sQuery(id+"F0.wireOp",EDGE,"E13.30.9"),sQuery(id+"F0.wireOp",EDGE,"E13.30.10"),sQuery(id+"F0.wireOp",EDGE,"E13.30.11"),sQuery(id+"F0.wireOp",EDGE,"E13.31.0"),sQuery(id+"F0.wireOp",EDGE,"E13.31.1"),sQuery(id+"F0.wireOp",EDGE,"E13.31.2"),sQuery(id+"F0.wireOp",EDGE,"E13.31.3"),sQuery(id+"F0.wireOp",EDGE,"E13.31.4"),sQuery(id+"F0.wireOp",EDGE,"E13.31.5"),sQuery(id+"F0.wireOp",EDGE,"E13.31.6"),sQuery(id+"F0.wireOp",EDGE,"E13.31.7"),sQuery(id+"F0.wireOp",EDGE,"E13.31.8"),sQuery(id+"F0.wireOp",EDGE,"E13.31.9"),sQuery(id+"F0.wireOp",EDGE,"E13.31.10"),sQuery(id+"F0.wireOp",EDGE,"E13.31.11"),sQuery(id+"F0.wireOp",EDGE,"E13.32.0"),sQuery(id+"F0.wireOp",EDGE,"E13.32.1"),sQuery(id+"F0.wireOp",EDGE,"E13.32.2"),sQuery(id+"F0.wireOp",EDGE,"E13.32.3"),sQuery(id+"F0.wireOp",EDGE,"E13.32.4"),sQuery(id+"F0.wireOp",EDGE,"E13.32.5"),sQuery(id+"F0.wireOp",EDGE,"E13.32.6"),sQuery(id+"F0.wireOp",EDGE,"E13.32.7"),sQuery(id+"F0.wireOp",EDGE,"E13.32.8"),sQuery(id+"F0.wireOp",EDGE,"E13.32.9"),sQuery(id+"F0.wireOp",EDGE,"E13.32.10"),sQuery(id+"F0.wireOp",EDGE,"E13.32.11"),sQuery(id+"F0.wireOp",EDGE,"E13.33.0"),sQuery(id+"F0.wireOp",EDGE,"E13.33.1"),sQuery(id+"F0.wireOp",EDGE,"E13.33.2"),sQuery(id+"F0.wireOp",EDGE,"E13.33.3"),sQuery(id+"F0.wireOp",EDGE,"E13.33.4"),sQuery(id+"F0.wireOp",EDGE,"E13.33.5"),sQuery(id+"F0.wireOp",EDGE,"E13.33.6"),sQuery(id+"F0.wireOp",EDGE,"E13.33.7"),sQuery(id+"F0.wireOp",EDGE,"E13.33.8"),sQuery(id+"F0.wireOp",EDGE,"E13.33.9"),sQuery(id+"F0.wireOp",EDGE,"E13.33.10"),sQuery(id+"F0.wireOp",EDGE,"E13.33.11"),sQuery(id+"F0.wireOp",EDGE,"E13.34.0"),sQuery(id+"F0.wireOp",EDGE,"E13.34.1"),sQuery(id+"F0.wireOp",EDGE,"E13.34.2"),sQuery(id+"F0.wireOp",EDGE,"E13.34.3"),sQuery(id+"F0.wireOp",EDGE,"E13.34.4"),sQuery(id+"F0.wireOp",EDGE,"E13.34.5"),sQuery(id+"F0.wireOp",EDGE,"E13.34.6"),sQuery(id+"F0.wireOp",EDGE,"E13.34.7"),sQuery(id+"F0.wireOp",EDGE,"E13.34.8"),sQuery(id+"F0.wireOp",EDGE,"E13.34.9"),sQuery(id+"F0.wireOp",EDGE,"E13.34.10"),sQuery(id+"F0.wireOp",EDGE,"E13.34.11"),sQuery(id+"F0.wireOp",EDGE,"E13.35.0"),sQuery(id+"F0.wireOp",EDGE,"E13.35.1"),sQuery(id+"F0.wireOp",EDGE,"E13.35.2"),sQuery(id+"F0.wireOp",EDGE,"E13.35.3"),sQuery(id+"F0.wireOp",EDGE,"E13.35.4"),sQuery(id+"F0.wireOp",EDGE,"E13.35.5"),sQuery(id+"F0.wireOp",EDGE,"E13.35.6"),sQuery(id+"F0.wireOp",EDGE,"E13.35.7"),sQuery(id+"F0.wireOp",EDGE,"E13.35.8"),sQuery(id+"F0.wireOp",EDGE,"E13.35.9"),sQuery(id+"F0.wireOp",EDGE,"E13.35.10"),sQuery(id+"F0.wireOp",EDGE,"E13.35.11"),sQuery(id+"F0.wireOp",EDGE,"E14.trimOffspring"),sQuery(id+"F0.wireOp",EDGE,"E15.trimOffspring"),sQuery(id+"F0.wireOp",EDGE,"E16.trimOffspring"),sQuery(id+"F0.wireOp",EDGE,"E17.trimOffspring"),sQuery(id+"F0.wireOp",EDGE,"E18.trimOffspring"),sQuery(id+"F0.wireOp",EDGE,"E19.trimOffspring"),sQuery(id+"F0.wireOp",EDGE,"E20.trimOffspring"),sQuery(id+"F0.wireOp",EDGE,"E21.trimOffspring"),sQuery(id+"F0.wireOp",EDGE,"E22.trimOffspring"),sQuery(id+"F0.wireOp",EDGE,"E23.trimOffspring"),sQuery(id+"F0.wireOp",EDGE,"E24.trimOffspring"),sQuery(id+"F0.wireOp",EDGE,"E25.trimOffspring"),sQuery(id+"F0.wireOp",EDGE,"E26.trimOffspring"),sQuery(id+"F0.wireOp",EDGE,"E27.trimOffspring"),sQuery(id+"F0.wireOp",EDGE,"E28.trimOffspring"),sQuery(id+"F0.wireOp",EDGE,"E29.trimOffspring"),sQuery(id+"F0.wireOp",EDGE,"E30.trimOffspring"),sQuery(id+"F0.wireOp",EDGE,"E31.trimOffspring"),sQuery(id+"F0.wireOp",EDGE,"E32.trimOffspring"),sQuery(id+"F0.wireOp",EDGE,"E33.trimOffspring"),sQuery(id+"F0.wireOp",EDGE,"E34.trimOffspring"),sQuery(id+"F0.wireOp",EDGE,"E35.trimOffspring"),sQuery(id+"F0.wireOp",EDGE,"E36.trimOffspring"),sQuery(id+"F0.wireOp",EDGE,"E37.trimOffspring"),sQuery(id+"F0.wireOp",EDGE,"E38.trimOffspring"),sQuery(id+"F0.wireOp",EDGE,"E39.trimOffspring"),sQuery(id+"F0.wireOp",EDGE,"E40.trimOffspring"),sQuery(id+"F0.wireOp",EDGE,"E41.trimOffspring"),sQuery(id+"F0.wireOp",EDGE,"E42.trimOffspring"),sQuery(id+"F0.wireOp",EDGE,"E43.trimOffspring"),sQuery(id+"F0.wireOp",EDGE,"E44.trimOffspring"),sQuery(id+"F0.wireOp",EDGE,"E45.trimOffspring"),sQuery(id+"F0.wireOp",EDGE,"E46.trimOffspring"),sQuery(id+"F0.wireOp",EDGE,"E47.trimOffspring"),sQuery(id+"F0.wireOp",EDGE,"E48.trimOffspring"),sQuery(id+"F0.wireOp",EDGE,"E49")])]});
            var sketch = newSketch(context, id + "F3", { "sketchPlane" : qUnion([Q0])});
            skCircle(sketch, "E50", {"center": v(0, 0) * mm, "radius": 3.18 * mm});
            skCircle(sketch, "E51", {"center": v(0, 0) * mm, "radius": 6.35 * mm});
            skSolve(sketch);
        }
        {
            var Q0;
            Q0=makeQuery(id+"F3.imprint","IMPRINT",FACE,{"disambiguationData":[TD([[makeQuery(id+"F3.imprint","IMPRINT",EDGE,{"derivedFrom":sQuery(id+"F3.wireOp",EDGE,"E50")}),1.0]])]});
            extrude(context, id + "F4", {"entities" : qUnion([Q0]), "operationType" : NewBodyOperationType.REMOVE, "endBound" : BoundingType.THROUGH_ALL, "oppositeDirection" : true, "depth" : 25.4 * mm});
        }
        {
            var Q0;
            Q0=makeQuery(id+"F3.imprint","IMPRINT",FACE,{"disambiguationData":[TD([[makeQuery(id+"F3.imprint","IMPRINT",EDGE,{"derivedFrom":sQuery(id+"F3.wireOp",EDGE,"E50")}),-1.0]])]});
            extrude(context, id + "F5", {"entities" : qUnion([Q0]), "operationType" : NewBodyOperationType.ADD, "depth" : 6.35 * mm});
        }
    });
